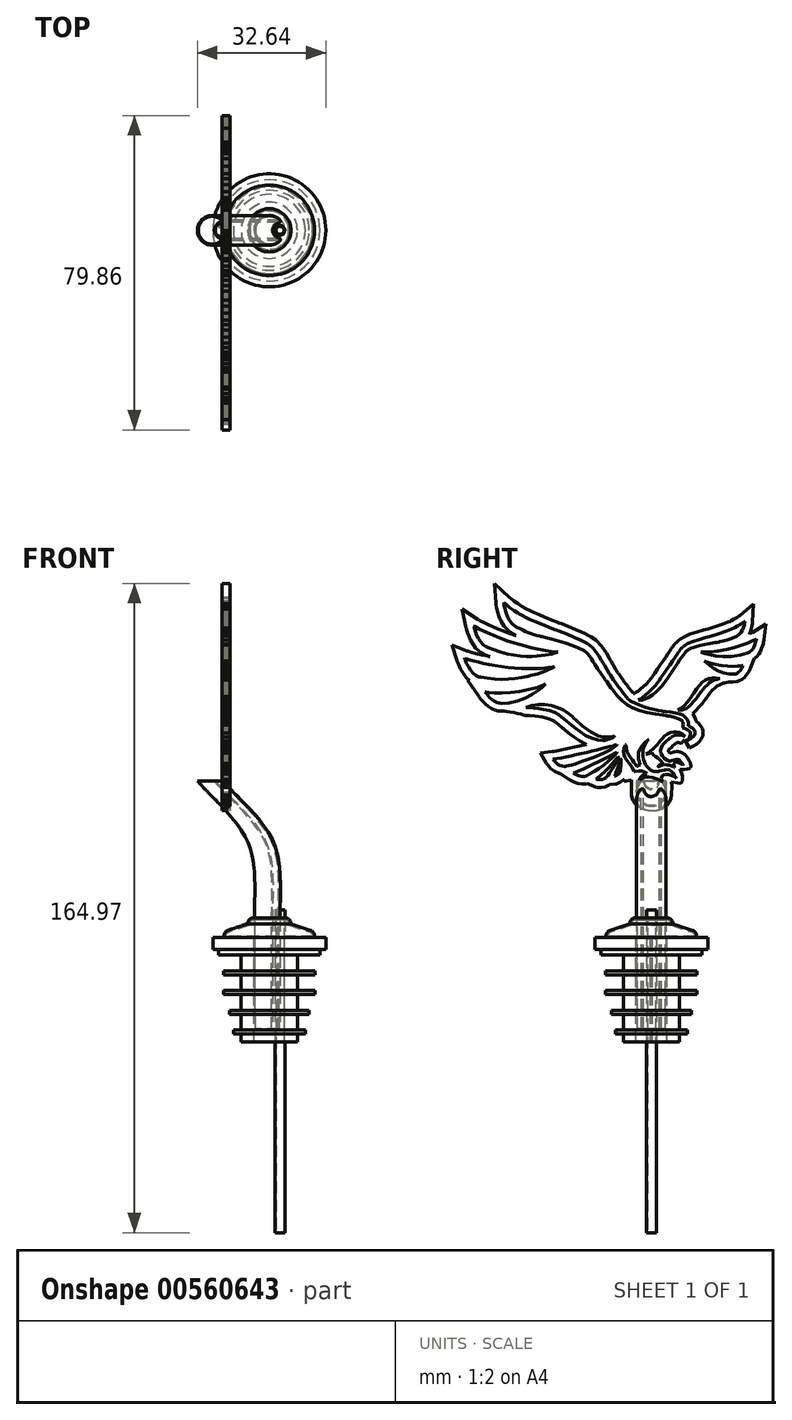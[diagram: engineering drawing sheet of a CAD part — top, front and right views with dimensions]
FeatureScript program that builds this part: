
annotation { "Feature Type Name" : "Feature", "Feature Type Description" : "" }
export const myFeature = defineFeature(function(context is Context, id is Id, definition is map)
    precondition{}
    {
        {
            var Q0;
            Q0=qCreatedBy(makeId("Top.planeOp"),FACE);
            var sketch = newSketch(context, id + "F0", { "sketchPlane" : qUnion([Q0])});
            skCircle(sketch, "E0", {"center": v(0, 0) * mm, "radius": 11.5 * mm});
            skSolve(sketch);
        }
        {
            var Q0;
            Q0=makeQuery(id+"F0.imprint","IMPRINT",FACE,{"disambiguationData":[TD([[makeQuery(id+"F0.imprint","IMPRINT",EDGE,{"derivedFrom":sQuery(id+"F0.wireOp",EDGE,"E0")}),1.0]])]});
            extrude(context, id + "F1", {"entities" : qUnion([Q0]), "depth" : 3.5 * mm, "offsetDistance" : 25 * mm});
        }
        {
            var Q0;
            Q0=makeQuery(id+"F1.opExtrude","CAP_FACE",FACE,{"disambiguationData":[OSD([sQuery(id+"F0.wireOp",EDGE,"E0")])],"isStart":false});
            chamfer(context, id + "F2", {"entities" : qUnion([Q0]), "chamferType" : ChamferType.TWO_OFFSETS, "width1" : 6 * mm, "oppositeDirection" : false, "width2" : 2 * mm, "tangentPropagation" : true});
        }
        {
            var Q0;
            Q0=makeQuery(id+"F1.opExtrude","CAP_FACE",FACE,{"disambiguationData":[OSD([sQuery(id+"F0.wireOp",EDGE,"E0")])],"isStart":false});
            var sketch = newSketch(context, id + "F3", { "sketchPlane" : qUnion([Q0])});
            skCircle(sketch, "E1", {"center": v(0, 0) * mm, "radius": 5.5 * mm});
            skSolve(sketch);
        }
        {
            var Q0;
            Q0=makeQuery(id+"F3.imprint","IMPRINT",FACE,{"disambiguationData":[TD([[makeQuery(id+"F3.imprint","IMPRINT",EDGE,{"derivedFrom":sQuery(id+"F3.wireOp",EDGE,"E1")}),1.0]])]});
            extrude(context, id + "F4", {"entities" : qUnion([Q0]), "operationType" : NewBodyOperationType.ADD, "depth" : 1.5 * mm, "offsetDistance" : 25 * mm});
        }
        {
            var Q0;
            Q0=makeQuery(id+"F4.opExtrude","CAP_EDGE",EDGE,{"disambiguationData":[OSD([sQuery(id+"F3.wireOp",EDGE,"E1")])],"isStart":false});
            fillet(context, id + "F5", {"entities" : qUnion([Q0]), "radius" : 1.5 * mm, "tangentPropagation" : true, "allowEdgeOverflow" : false});
        }
        {
            var Q0;
            {var subQ0=sQuery(id+"F0.wireOp",EDGE,"E0");Q0=makeQuery(id+"F2.opChamfer","BLEND_EDGE",EDGE,{"blendedFrom":[makeQuery(id+"F1.opExtrude","CAP_EDGE",EDGE,{"disambiguationData":[OSD([subQ0])],"isStart":false}),makeQuery(id+"F1.opExtrude","SWEPT_FACE",FACE,{"disambiguationData":[OSD([subQ0])]})],"blendedInto":[makeQuery(id+"F1.opExtrude","SWEPT_FACE",FACE,{"disambiguationData":[OSD([subQ0])]})]});}
            fillet(context, id + "F6", {"entities" : qUnion([Q0]), "radius" : 1.5 * mm, "tangentPropagation" : true, "allowEdgeOverflow" : false});
        }
        {
            var Q0;
            Q0=makeQuery(id+"F1.opExtrude","CAP_FACE",FACE,{"disambiguationData":[OSD([sQuery(id+"F0.wireOp",EDGE,"E0")])],"isStart":true});
            shell(context, id + "F7", {"entities" : qUnion([Q0]), "thickness" : 0.5 * mm});
        }
        {
            var Q0;
            Q0=qCreatedBy(makeId("Top.planeOp"),FACE);
            cPlane(context, id + "F8", {"entities" : qUnion([Q0]), "cplaneType" : CPlaneType.OFFSET, "offset" : 75 * mm, "oppositeDirection" : true, "width" : 150 * mm, "height" : 150 * mm});
        }
        {
            var Q0;
            Q0=qCreatedBy(id+"F8.planeOp",FACE);
            var sketch = newSketch(context, id + "F9", { "sketchPlane" : qUnion([Q0])});
            skCircle(sketch, "E2", {"center": v(2.7, 0) * mm, "radius": 1.25 * mm});
            skSolve(sketch);
        }
        {
            var Q0;
            Q0=makeQuery(id+"F9.imprint","IMPRINT",FACE,{"disambiguationData":[TD([[makeQuery(id+"F9.imprint","IMPRINT",EDGE,{"derivedFrom":sQuery(id+"F9.wireOp",EDGE,"E2")}),1.0]])]});
            extrude(context, id + "F10", {"entities" : qUnion([Q0]), "operationType" : NewBodyOperationType.ADD, "depth" : 82 * mm, "offsetDistance" : 25 * mm});
        }
        {
            var Q0;
            Q0=makeQuery(id+"F10.opExtrude","CAP_FACE",FACE,{"disambiguationData":[OSD([sQuery(id+"F9.wireOp",EDGE,"E2")])],"isStart":false});
            var Q1;
            Q1=makeQuery(id+"F10.opExtrude","CAP_FACE",FACE,{"disambiguationData":[OSD([sQuery(id+"F9.wireOp",EDGE,"E2")])],"isStart":true});
            shell(context, id + "F11", {"entities" : qUnion([Q0, Q1]), "thickness" : 0.25 * mm});
        }
        {
            var Q0;
            Q0=qCreatedBy(makeId("Top.planeOp"),FACE);
            cPlane(context, id + "F12", {"entities" : qUnion([Q0]), "cplaneType" : CPlaneType.OFFSET, "offset" : 23 * mm, "oppositeDirection" : true, "width" : 150 * mm, "height" : 150 * mm});
        }
        {
            var Q0;
            Q0=qCreatedBy(id+"F12.planeOp",FACE);
            var sketch = newSketch(context, id + "F13", { "sketchPlane" : qUnion([Q0])});
            skArc(sketch, "E3", {"start": v(2.59, 2.71) * mm, "mid": v(-3.75, 0) * mm, "end": v(2.59, -2.71) * mm});
            skArc(sketch, "E4", {"start": v(2.34, 1.86) * mm, "mid": v(0.82, 0) * mm, "end": v(2.34, -1.86) * mm});
            skPoint(sketch, "E5.visualSharp", {"position": v(3.28, 1.81) * mm});
            skArc(sketch, "E5.filletArc", {"start": v(2.34, 1.86) * mm, "mid": v(2.72, 2.21) * mm, "end": v(2.59, 2.71) * mm});
            skPoint(sketch, "E6.visualSharp", {"position": v(3.28, -1.81) * mm});
            skArc(sketch, "E6.filletArc", {"start": v(2.59, -2.71) * mm, "mid": v(2.72, -2.21) * mm, "end": v(2.34, -1.86) * mm});
            skSolve(sketch);
        }
        {
            var Q0;
            Q0=qCreatedBy(makeId("Top.planeOp"),FACE);
            cPlane(context, id + "F14", {"entities" : qUnion([Q0]), "cplaneType" : CPlaneType.OFFSET, "offset" : 15 * mm, "width" : 150 * mm, "height" : 150 * mm});
        }
        {
            var Q0;
            Q0=qCreatedBy(makeId("Front.planeOp"),FACE);
            var sketch = newSketch(context, id + "F15", { "sketchPlane" : qUnion([Q0])});
            skFitSpline(sketch, "E7", {"points": [v(0, -23.23) * mm, v(0, 6.5) * mm, v(0, 15.7) * mm, v(-2.95, 26.7) * mm, v(-14.54, 39.77) * mm], "startDerivative": vector(-0.7, 126.33) * mm, "endDerivative": vector(-30.29, 36.58) * mm});
            skSolve(sketch);
        }
        {
            var Q0;
            Q0=makeQuery(id+"F13.imprint","IMPRINT",FACE,{"disambiguationData":[TD([[makeQuery(id+"F13.imprint","IMPRINT",EDGE,{"derivedFrom":sQuery(id+"F13.wireOp",EDGE,"E3")}),1.0]])]});
            var Q1;
            Q1=sQuery(id+"F15.wireOp",EDGE,"E7");
            sweep(context, id + "F16", {"operationType" : NewBodyOperationType.ADD, "profiles" : qUnion([Q0]), "path" : qUnion([Q1]), "keepProfileOrientation" : true});
        }
        {
            var Q0;
            Q0=makeQuery(id+"F16.opSweep","CAP_FACE",FACE,{"disambiguationData":[OSD([sQuery(id+"F13.wireOp",EDGE,"E3"),sQuery(id+"F13.wireOp",EDGE,"E4"),sQuery(id+"F13.wireOp",EDGE,"E5.filletArc"),sQuery(id+"F13.wireOp",EDGE,"E6.filletArc"),sQuery(id+"F15.wireOp",VERTEX,"E7.end")])],"isStart":false});
            var Q1;
            Q1=makeQuery(id+"F16.opSweep","CAP_FACE",FACE,{"disambiguationData":[OSD([sQuery(id+"F13.wireOp",EDGE,"E3"),sQuery(id+"F13.wireOp",EDGE,"E4"),sQuery(id+"F13.wireOp",EDGE,"E5.filletArc"),sQuery(id+"F13.wireOp",EDGE,"E6.filletArc"),sQuery(id+"F15.wireOp",VERTEX,"E7.start")])],"isStart":true});
            shell(context, id + "F17", {"entities" : qUnion([Q0, Q1]), "thickness" : 0.2 * mm});
        }
        {
            var Q0;
            Q0=qCreatedBy(makeId("Right.planeOp"),FACE);
            var sketch = newSketch(context, id + "F18", { "sketchPlane" : qUnion([Q0])});
            skLineSegment(sketch, "E8", {"start": v(-3.93, -22.94) * mm, "end": v(-3.93, 0) * mm});
            skLineSegment(sketch, "E9", {"start": v(-3.93, 0) * mm, "end": v(-14.35, 0) * mm});
            skLineSegment(sketch, "E10", {"start": v(-14.35, 0) * mm, "end": v(-14.35, -3) * mm});
            skLineSegment(sketch, "E11", {"start": v(-14.35, -3) * mm, "end": v(-12.85, -3) * mm});
            skLineSegment(sketch, "E12", {"start": v(-12.85, -3) * mm, "end": v(-12.85, -4.5) * mm});
            skLineSegment(sketch, "E13", {"start": v(-12.85, -4.5) * mm, "end": v(-7.14, -4.5) * mm});
            skLineSegment(sketch, "E14", {"start": v(-7.14, -4.5) * mm, "end": v(-7.14, -8.5) * mm});
            skLineSegment(sketch, "E15", {"start": v(-7.14, -8.5) * mm, "end": v(-11.64, -8.5) * mm});
            skLineSegment(sketch, "E16", {"start": v(-11.64, -8.5) * mm, "end": v(-11.64, -9.5) * mm});
            skLineSegment(sketch, "E17", {"start": v(-11.64, -9.5) * mm, "end": v(-7.14, -9.5) * mm});
            skLineSegment(sketch, "E18", {"start": v(-7.14, -9.5) * mm, "end": v(-7.14, -13.5) * mm});
            skLineSegment(sketch, "E19", {"start": v(-7.14, -13.5) * mm, "end": v(-11.64, -13.5) * mm});
            skLineSegment(sketch, "E20", {"start": v(-11.64, -13.5) * mm, "end": v(-11.64, -14.5) * mm});
            skLineSegment(sketch, "E21", {"start": v(-11.64, -14.5) * mm, "end": v(-7.14, -14.5) * mm});
            skLineSegment(sketch, "E22", {"start": v(-7.14, -14.5) * mm, "end": v(-7.14, -18.5) * mm});
            skLineSegment(sketch, "E23", {"start": v(-7.14, -18.5) * mm, "end": v(-10.14, -18.5) * mm});
            skLineSegment(sketch, "E24", {"start": v(-10.14, -18.5) * mm, "end": v(-10.14, -19.5) * mm});
            skLineSegment(sketch, "E25", {"start": v(-10.14, -19.5) * mm, "end": v(-7.14, -19.5) * mm});
            skLineSegment(sketch, "E26", {"start": v(-7.14, -19.5) * mm, "end": v(-7.14, -23.5) * mm});
            skLineSegment(sketch, "E27", {"start": v(-7.14, -23.5) * mm, "end": v(-9.14, -23.5) * mm});
            skLineSegment(sketch, "E28", {"start": v(-9.14, -23.5) * mm, "end": v(-9.14, -24.5) * mm});
            skLineSegment(sketch, "E29", {"start": v(-9.14, -24.5) * mm, "end": v(-7.14, -24.5) * mm});
            skLineSegment(sketch, "E30", {"start": v(-7.14, -24.5) * mm, "end": v(-7.14, -26.5) * mm});
            skLineSegment(sketch, "E31", {"start": v(-7.14, -26.5) * mm, "end": v(-3.93, -26.5) * mm});
            skLineSegment(sketch, "E32", {"start": v(-3.93, -26.5) * mm, "end": v(-3.93, -22.94) * mm});
            skLineSegment(sketch, "E33", {"start": v(0, 0) * mm, "end": v(0, -26.54) * mm});
            skSolve(sketch);
        }
        {
            var Q0;
            Q0=makeQuery(id+"F18.imprint","IMPRINT",FACE,{"disambiguationData":[TD([[makeQuery(id+"F18.imprint","IMPRINT",EDGE,{"derivedFrom":sQuery(id+"F18.wireOp",EDGE,"E8")}),1.0]])]});
            var Q1;
            Q1=sQuery(id+"F18.wireOp",EDGE,"E33");
            revolve(context, id + "F19", {"operationType" : NewBodyOperationType.ADD, "entities" : qUnion([Q0]), "axis" : qUnion([Q1]), "revolveType" : RevolveType.FULL});
        }
        {
            var Q0;
            Q0=qCreatedBy(makeId("Right.planeOp"),FACE);
            cPlane(context, id + "F20", {"entities" : qUnion([Q0]), "cplaneType" : CPlaneType.OFFSET, "offset" : 12 * mm, "oppositeDirection" : true, "width" : 150 * mm, "height" : 150 * mm});
        }
        {
            var Q0;
            Q0=qCreatedBy(id+"F20.planeOp",FACE);
            var sketch = newSketch(context, id + "F21", { "sketchPlane" : qUnion([Q0])});
            skLineSegment(sketch, "E34", {"start": v(24.98, 72.56) * mm, "end": v(24.4, 72.32) * mm});
            skLineSegment(sketch, "E35", {"start": v(24.4, 72.32) * mm, "end": v(22.61, 71.8) * mm});
            skLineSegment(sketch, "E36", {"start": v(22.61, 71.8) * mm, "end": v(20.35, 71.44) * mm});
            skLineSegment(sketch, "E37", {"start": v(20.35, 71.44) * mm, "end": v(18.25, 71.39) * mm});
            skLineSegment(sketch, "E38", {"start": v(18.25, 71.39) * mm, "end": v(16.38, 71.55) * mm});
            skLineSegment(sketch, "E39", {"start": v(16.38, 71.55) * mm, "end": v(14.81, 71.84) * mm});
            skLineSegment(sketch, "E40", {"start": v(14.81, 71.84) * mm, "end": v(13.6, 72.17) * mm});
            skLineSegment(sketch, "E41", {"start": v(13.6, 72.17) * mm, "end": v(12.84, 72.43) * mm});
            skLineSegment(sketch, "E42", {"start": v(12.84, 72.43) * mm, "end": v(12.57, 72.54) * mm});
            skLineSegment(sketch, "E43", {"start": v(12.57, 72.54) * mm, "end": v(13.1, 72.5) * mm});
            skLineSegment(sketch, "E44", {"start": v(13.1, 72.5) * mm, "end": v(14.73, 72.54) * mm});
            skLineSegment(sketch, "E45", {"start": v(14.73, 72.54) * mm, "end": v(16.92, 72.76) * mm});
            skLineSegment(sketch, "E46", {"start": v(16.92, 72.76) * mm, "end": v(19.08, 73.17) * mm});
            skLineSegment(sketch, "E47", {"start": v(19.08, 73.17) * mm, "end": v(21.13, 73.7) * mm});
            skLineSegment(sketch, "E48", {"start": v(21.13, 73.7) * mm, "end": v(22.98, 74.28) * mm});
            skLineSegment(sketch, "E49", {"start": v(22.98, 74.28) * mm, "end": v(24.57, 74.87) * mm});
            skLineSegment(sketch, "E50", {"start": v(24.57, 74.87) * mm, "end": v(25.82, 75.42) * mm});
            skLineSegment(sketch, "E51", {"start": v(25.82, 75.42) * mm, "end": v(26.46, 75.73) * mm});
            skLineSegment(sketch, "E52", {"start": v(26.46, 75.73) * mm, "end": v(26.66, 75.85) * mm});
            skLineSegment(sketch, "E53", {"start": v(26.66, 75.85) * mm, "end": v(26.64, 75.73) * mm});
            skLineSegment(sketch, "E54", {"start": v(26.64, 75.73) * mm, "end": v(26.58, 75.42) * mm});
            skLineSegment(sketch, "E55", {"start": v(26.58, 75.42) * mm, "end": v(26.47, 74.96) * mm});
            skLineSegment(sketch, "E56", {"start": v(26.47, 74.96) * mm, "end": v(26.3, 74.41) * mm});
            skLineSegment(sketch, "E57", {"start": v(26.3, 74.41) * mm, "end": v(26.08, 73.84) * mm});
            skLineSegment(sketch, "E58", {"start": v(26.08, 73.84) * mm, "end": v(25.8, 73.3) * mm});
            skLineSegment(sketch, "E59", {"start": v(25.8, 73.3) * mm, "end": v(25.43, 72.86) * mm});
            skLineSegment(sketch, "E60", {"start": v(25.43, 72.86) * mm, "end": v(25.1, 72.61) * mm});
            skLineSegment(sketch, "E61", {"start": v(25.1, 72.61) * mm, "end": v(24.98, 72.56) * mm});
            skLineSegment(sketch, "E62", {"start": v(21.4, 66.97) * mm, "end": v(21.02, 66.9) * mm});
            skLineSegment(sketch, "E63", {"start": v(21.02, 66.9) * mm, "end": v(19.86, 66.91) * mm});
            skLineSegment(sketch, "E64", {"start": v(19.86, 66.91) * mm, "end": v(18.4, 67.2) * mm});
            skLineSegment(sketch, "E65", {"start": v(18.4, 67.2) * mm, "end": v(17.06, 67.72) * mm});
            skLineSegment(sketch, "E66", {"start": v(17.06, 67.72) * mm, "end": v(15.87, 68.38) * mm});
            skLineSegment(sketch, "E67", {"start": v(15.87, 68.38) * mm, "end": v(14.88, 69.07) * mm});
            skLineSegment(sketch, "E68", {"start": v(14.88, 69.07) * mm, "end": v(14.13, 69.69) * mm});
            skLineSegment(sketch, "E69", {"start": v(14.13, 69.69) * mm, "end": v(13.65, 70.13) * mm});
            skLineSegment(sketch, "E70", {"start": v(13.65, 70.13) * mm, "end": v(13.48, 70.3) * mm});
            skLineSegment(sketch, "E71", {"start": v(13.48, 70.3) * mm, "end": v(13.81, 70.13) * mm});
            skLineSegment(sketch, "E72", {"start": v(13.81, 70.13) * mm, "end": v(14.87, 69.72) * mm});
            skLineSegment(sketch, "E73", {"start": v(14.87, 69.72) * mm, "end": v(16.36, 69.31) * mm});
            skLineSegment(sketch, "E74", {"start": v(16.36, 69.31) * mm, "end": v(17.87, 69.05) * mm});
            skLineSegment(sketch, "E75", {"start": v(17.87, 69.05) * mm, "end": v(19.33, 68.92) * mm});
            skLineSegment(sketch, "E76", {"start": v(19.33, 68.92) * mm, "end": v(20.67, 68.88) * mm});
            skLineSegment(sketch, "E77", {"start": v(20.67, 68.88) * mm, "end": v(21.83, 68.93) * mm});
            skLineSegment(sketch, "E78", {"start": v(21.83, 68.93) * mm, "end": v(22.73, 69.02) * mm});
            skLineSegment(sketch, "E79", {"start": v(22.73, 69.02) * mm, "end": v(23.17, 69.1) * mm});
            skLineSegment(sketch, "E80", {"start": v(23.17, 69.1) * mm, "end": v(23.31, 69.15) * mm});
            skLineSegment(sketch, "E81", {"start": v(23.31, 69.15) * mm, "end": v(23.27, 69.06) * mm});
            skLineSegment(sketch, "E82", {"start": v(23.27, 69.06) * mm, "end": v(23.17, 68.83) * mm});
            skLineSegment(sketch, "E83", {"start": v(23.17, 68.83) * mm, "end": v(23, 68.5) * mm});
            skLineSegment(sketch, "E84", {"start": v(23, 68.5) * mm, "end": v(22.77, 68.12) * mm});
            skLineSegment(sketch, "E85", {"start": v(22.77, 68.12) * mm, "end": v(22.5, 67.74) * mm});
            skLineSegment(sketch, "E86", {"start": v(22.5, 67.74) * mm, "end": v(22.17, 67.38) * mm});
            skLineSegment(sketch, "E87", {"start": v(22.17, 67.38) * mm, "end": v(21.8, 67.11) * mm});
            skLineSegment(sketch, "E88", {"start": v(21.8, 67.11) * mm, "end": v(21.5, 66.98) * mm});
            skLineSegment(sketch, "E89", {"start": v(21.5, 66.98) * mm, "end": v(21.4, 66.97) * mm});
            skLineSegment(sketch, "E90", {"start": v(11.79, 61.24) * mm, "end": v(11.67, 61.08) * mm});
            skLineSegment(sketch, "E91", {"start": v(11.67, 61.08) * mm, "end": v(11.3, 60.59) * mm});
            skLineSegment(sketch, "E92", {"start": v(11.3, 60.59) * mm, "end": v(10.75, 59.91) * mm});
            skLineSegment(sketch, "E93", {"start": v(10.75, 59.91) * mm, "end": v(10.16, 59.26) * mm});
            skLineSegment(sketch, "E94", {"start": v(10.16, 59.26) * mm, "end": v(9.53, 58.67) * mm});
            skLineSegment(sketch, "E95", {"start": v(9.53, 58.67) * mm, "end": v(8.87, 58.2) * mm});
            skLineSegment(sketch, "E96", {"start": v(8.87, 58.2) * mm, "end": v(8.18, 57.86) * mm});
            skLineSegment(sketch, "E97", {"start": v(8.18, 57.86) * mm, "end": v(7.48, 57.72) * mm});
            skLineSegment(sketch, "E98", {"start": v(7.48, 57.72) * mm, "end": v(6.93, 57.76) * mm});
            skLineSegment(sketch, "E99", {"start": v(6.93, 57.76) * mm, "end": v(6.76, 57.81) * mm});
            skLineSegment(sketch, "E100", {"start": v(6.76, 57.81) * mm, "end": v(6.94, 57.86) * mm});
            skLineSegment(sketch, "E101", {"start": v(6.94, 57.86) * mm, "end": v(7.45, 58.12) * mm});
            skLineSegment(sketch, "E102", {"start": v(7.45, 58.12) * mm, "end": v(8.3, 58.8) * mm});
            skLineSegment(sketch, "E103", {"start": v(8.3, 58.8) * mm, "end": v(9.34, 60) * mm});
            skLineSegment(sketch, "E104", {"start": v(9.34, 60) * mm, "end": v(10.32, 61.38) * mm});
            skLineSegment(sketch, "E105", {"start": v(10.32, 61.38) * mm, "end": v(10.62, 61.86) * mm});
            skLineSegment(sketch, "E106", {"start": v(10.62, 61.86) * mm, "end": v(10.82, 62.17) * mm});
            skLineSegment(sketch, "E107", {"start": v(10.82, 62.17) * mm, "end": v(11.44, 63.08) * mm});
            skLineSegment(sketch, "E108", {"start": v(11.44, 63.08) * mm, "end": v(12.22, 64.08) * mm});
            skLineSegment(sketch, "E109", {"start": v(12.22, 64.08) * mm, "end": v(12.99, 64.86) * mm});
            skLineSegment(sketch, "E110", {"start": v(12.99, 64.86) * mm, "end": v(13.77, 65.43) * mm});
            skLineSegment(sketch, "E111", {"start": v(13.77, 65.43) * mm, "end": v(14.58, 65.8) * mm});
            skLineSegment(sketch, "E112", {"start": v(14.58, 65.8) * mm, "end": v(15.45, 65.98) * mm});
            skLineSegment(sketch, "E113", {"start": v(15.45, 65.98) * mm, "end": v(16.4, 65.98) * mm});
            skLineSegment(sketch, "E114", {"start": v(16.4, 65.98) * mm, "end": v(17.2, 65.85) * mm});
            skLineSegment(sketch, "E115", {"start": v(17.2, 65.85) * mm, "end": v(17.45, 65.8) * mm});
            skLineSegment(sketch, "E116", {"start": v(17.45, 65.8) * mm, "end": v(17.26, 65.74) * mm});
            skLineSegment(sketch, "E117", {"start": v(17.26, 65.74) * mm, "end": v(16.68, 65.6) * mm});
            skLineSegment(sketch, "E118", {"start": v(16.68, 65.6) * mm, "end": v(16.02, 65.38) * mm});
            skLineSegment(sketch, "E119", {"start": v(16.02, 65.38) * mm, "end": v(15.4, 65.1) * mm});
            skLineSegment(sketch, "E120", {"start": v(15.4, 65.1) * mm, "end": v(14.82, 64.72) * mm});
            skLineSegment(sketch, "E121", {"start": v(14.82, 64.72) * mm, "end": v(14.21, 64.18) * mm});
            skLineSegment(sketch, "E122", {"start": v(14.21, 64.18) * mm, "end": v(13.53, 63.46) * mm});
            skLineSegment(sketch, "E123", {"start": v(13.53, 63.46) * mm, "end": v(12.74, 62.49) * mm});
            skLineSegment(sketch, "E124", {"start": v(12.74, 62.49) * mm, "end": v(12.02, 61.56) * mm});
            skLineSegment(sketch, "E125", {"start": v(12.02, 61.56) * mm, "end": v(11.79, 61.24) * mm});
            skLineSegment(sketch, "E126", {"start": v(8.94, 49.98) * mm, "end": v(8.99, 50.02) * mm});
            skLineSegment(sketch, "E127", {"start": v(8.99, 50.02) * mm, "end": v(9.12, 50.13) * mm});
            skLineSegment(sketch, "E128", {"start": v(9.12, 50.13) * mm, "end": v(9.3, 50.32) * mm});
            skLineSegment(sketch, "E129", {"start": v(9.3, 50.32) * mm, "end": v(9.5, 50.55) * mm});
            skLineSegment(sketch, "E130", {"start": v(9.5, 50.55) * mm, "end": v(9.7, 50.84) * mm});
            skLineSegment(sketch, "E131", {"start": v(9.7, 50.84) * mm, "end": v(9.86, 51.16) * mm});
            skLineSegment(sketch, "E132", {"start": v(9.86, 51.16) * mm, "end": v(9.95, 51.5) * mm});
            skLineSegment(sketch, "E133", {"start": v(9.95, 51.5) * mm, "end": v(9.96, 51.79) * mm});
            skLineSegment(sketch, "E134", {"start": v(9.96, 51.79) * mm, "end": v(9.95, 51.87) * mm});
            skLineSegment(sketch, "E135", {"start": v(9.95, 51.87) * mm, "end": v(9.93, 52) * mm});
            skLineSegment(sketch, "E136", {"start": v(9.93, 52) * mm, "end": v(9.75, 52.34) * mm});
            skLineSegment(sketch, "E137", {"start": v(9.75, 52.34) * mm, "end": v(9.35, 52.69) * mm});
            skLineSegment(sketch, "E138", {"start": v(9.35, 52.69) * mm, "end": v(8.75, 52.97) * mm});
            skLineSegment(sketch, "E139", {"start": v(8.75, 52.97) * mm, "end": v(8.13, 53.18) * mm});
            skLineSegment(sketch, "E140", {"start": v(8.13, 53.18) * mm, "end": v(7.93, 53.25) * mm});
            skLineSegment(sketch, "E141", {"start": v(7.93, 53.25) * mm, "end": v(7.97, 53.39) * mm});
            skLineSegment(sketch, "E142", {"start": v(7.97, 53.39) * mm, "end": v(8.06, 53.73) * mm});
            skLineSegment(sketch, "E143", {"start": v(8.06, 53.73) * mm, "end": v(8.1, 54.16) * mm});
            skLineSegment(sketch, "E144", {"start": v(8.1, 54.16) * mm, "end": v(8.08, 54.47) * mm});
            skLineSegment(sketch, "E145", {"start": v(8.08, 54.47) * mm, "end": v(8.05, 54.56) * mm});
            skLineSegment(sketch, "E146", {"start": v(8.05, 54.56) * mm, "end": v(8, 54.7) * mm});
            skLineSegment(sketch, "E147", {"start": v(8, 54.7) * mm, "end": v(7.72, 55.06) * mm});
            skLineSegment(sketch, "E148", {"start": v(7.72, 55.06) * mm, "end": v(7.07, 55.52) * mm});
            skLineSegment(sketch, "E149", {"start": v(7.07, 55.52) * mm, "end": v(5.99, 55.93) * mm});
            skLineSegment(sketch, "E150", {"start": v(5.99, 55.93) * mm, "end": v(4.77, 56.21) * mm});
            skLineSegment(sketch, "E151", {"start": v(4.77, 56.21) * mm, "end": v(4.36, 56.28) * mm});
            skLineSegment(sketch, "E152", {"start": v(4.36, 56.28) * mm, "end": v(4.33, 56.28) * mm});
            skLineSegment(sketch, "E153", {"start": v(4.33, 56.28) * mm, "end": v(3.99, 56.33) * mm});
            skLineSegment(sketch, "E154", {"start": v(3.99, 56.33) * mm, "end": v(3.95, 56.34) * mm});
            skLineSegment(sketch, "E155", {"start": v(3.95, 56.34) * mm, "end": v(3.93, 56.34) * mm});
            skLineSegment(sketch, "E156", {"start": v(3.93, 56.34) * mm, "end": v(3.66, 56.37) * mm});
            skLineSegment(sketch, "E157", {"start": v(3.66, 56.37) * mm, "end": v(3.63, 56.37) * mm});
            skLineSegment(sketch, "E158", {"start": v(3.63, 56.37) * mm, "end": v(2.98, 56.47) * mm});
            skLineSegment(sketch, "E159", {"start": v(2.98, 56.47) * mm, "end": v(1.04, 56.77) * mm});
            skLineSegment(sketch, "E160", {"start": v(1.04, 56.77) * mm, "end": v(-1.15, 57.18) * mm});
            skLineSegment(sketch, "E161", {"start": v(-1.15, 57.18) * mm, "end": v(-3.03, 57.66) * mm});
            skLineSegment(sketch, "E162", {"start": v(-3.03, 57.66) * mm, "end": v(-4.66, 58.28) * mm});
            skLineSegment(sketch, "E163", {"start": v(-4.66, 58.28) * mm, "end": v(-6.1, 59.09) * mm});
            skLineSegment(sketch, "E164", {"start": v(-6.1, 59.09) * mm, "end": v(-7.45, 60.15) * mm});
            skLineSegment(sketch, "E165", {"start": v(-7.45, 60.15) * mm, "end": v(-8.75, 61.52) * mm});
            skLineSegment(sketch, "E166", {"start": v(-8.75, 61.52) * mm, "end": v(-9.77, 62.81) * mm});
            skLineSegment(sketch, "E167", {"start": v(-9.77, 62.81) * mm, "end": v(-10.09, 63.26) * mm});
            skLineSegment(sketch, "E168", {"start": v(-10.09, 63.26) * mm, "end": v(-10.2, 63.43) * mm});
            skLineSegment(sketch, "E169", {"start": v(-10.2, 63.43) * mm, "end": v(-11.3, 64.99) * mm});
            skLineSegment(sketch, "E170", {"start": v(-11.3, 64.99) * mm, "end": v(-11.4, 65.13) * mm});
            skLineSegment(sketch, "E171", {"start": v(-11.4, 65.13) * mm, "end": v(-11.41, 65.15) * mm});
            skLineSegment(sketch, "E172", {"start": v(-11.41, 65.15) * mm, "end": v(-11.57, 65.37) * mm});
            skLineSegment(sketch, "E173", {"start": v(-11.57, 65.37) * mm, "end": v(-11.59, 65.4) * mm});
            skLineSegment(sketch, "E174", {"start": v(-11.59, 65.4) * mm, "end": v(-11.9, 65.81) * mm});
            skLineSegment(sketch, "E175", {"start": v(-11.9, 65.81) * mm, "end": v(-12.8, 67.08) * mm});
            skLineSegment(sketch, "E176", {"start": v(-12.8, 67.08) * mm, "end": v(-13.7, 68.4) * mm});
            skLineSegment(sketch, "E177", {"start": v(-13.7, 68.4) * mm, "end": v(-14.35, 69.39) * mm});
            skLineSegment(sketch, "E178", {"start": v(-14.35, 69.39) * mm, "end": v(-14.81, 70.14) * mm});
            skLineSegment(sketch, "E179", {"start": v(-14.81, 70.14) * mm, "end": v(-15.16, 70.73) * mm});
            skLineSegment(sketch, "E180", {"start": v(-15.16, 70.73) * mm, "end": v(-15.46, 71.2) * mm});
            skLineSegment(sketch, "E181", {"start": v(-15.46, 71.2) * mm, "end": v(-15.78, 71.64) * mm});
            skLineSegment(sketch, "E182", {"start": v(-15.78, 71.64) * mm, "end": v(-16.1, 72) * mm});
            skLineSegment(sketch, "E183", {"start": v(-16.1, 72) * mm, "end": v(-16.2, 72.12) * mm});
            skLineSegment(sketch, "E184", {"start": v(-16.2, 72.12) * mm, "end": v(-16.4, 72.33) * mm});
            skLineSegment(sketch, "E185", {"start": v(-16.4, 72.33) * mm, "end": v(-17.14, 72.85) * mm});
            skLineSegment(sketch, "E186", {"start": v(-17.14, 72.85) * mm, "end": v(-18.47, 73.54) * mm});
            skLineSegment(sketch, "E187", {"start": v(-18.47, 73.54) * mm, "end": v(-20.07, 74.2) * mm});
            skLineSegment(sketch, "E188", {"start": v(-20.07, 74.2) * mm, "end": v(-21.83, 74.79) * mm});
            skLineSegment(sketch, "E189", {"start": v(-21.83, 74.79) * mm, "end": v(-23.63, 75.32) * mm});
            skLineSegment(sketch, "E190", {"start": v(-23.63, 75.32) * mm, "end": v(-25.35, 75.79) * mm});
            skLineSegment(sketch, "E191", {"start": v(-25.35, 75.79) * mm, "end": v(-26.89, 76.18) * mm});
            skLineSegment(sketch, "E192", {"start": v(-26.89, 76.18) * mm, "end": v(-27.8, 76.4) * mm});
            skLineSegment(sketch, "E193", {"start": v(-27.8, 76.4) * mm, "end": v(-28.11, 76.48) * mm});
            skLineSegment(sketch, "E194", {"start": v(-28.11, 76.48) * mm, "end": v(-28.35, 76.54) * mm});
            skLineSegment(sketch, "E195", {"start": v(-28.35, 76.54) * mm, "end": v(-29.08, 76.73) * mm});
            skLineSegment(sketch, "E196", {"start": v(-29.08, 76.73) * mm, "end": v(-29.9, 76.96) * mm});
            skLineSegment(sketch, "E197", {"start": v(-29.9, 76.96) * mm, "end": v(-30.62, 77.2) * mm});
            skLineSegment(sketch, "E198", {"start": v(-30.62, 77.2) * mm, "end": v(-31.3, 77.44) * mm});
            skLineSegment(sketch, "E199", {"start": v(-31.3, 77.44) * mm, "end": v(-31.95, 77.72) * mm});
            skLineSegment(sketch, "E200", {"start": v(-31.95, 77.72) * mm, "end": v(-32.65, 78.05) * mm});
            skLineSegment(sketch, "E201", {"start": v(-32.65, 78.05) * mm, "end": v(-33.41, 78.45) * mm});
            skLineSegment(sketch, "E202", {"start": v(-33.41, 78.45) * mm, "end": v(-34.08, 78.8) * mm});
            skLineSegment(sketch, "E203", {"start": v(-34.08, 78.8) * mm, "end": v(-34.3, 78.92) * mm});
            skLineSegment(sketch, "E204", {"start": v(-34.3, 78.92) * mm, "end": v(-34.56, 79.06) * mm});
            skLineSegment(sketch, "E205", {"start": v(-34.56, 79.06) * mm, "end": v(-35.25, 79.62) * mm});
            skLineSegment(sketch, "E206", {"start": v(-35.25, 79.62) * mm, "end": v(-36, 80.53) * mm});
            skLineSegment(sketch, "E207", {"start": v(-36, 80.53) * mm, "end": v(-36.56, 81.54) * mm});
            skLineSegment(sketch, "E208", {"start": v(-36.56, 81.54) * mm, "end": v(-36.96, 82.58) * mm});
            skLineSegment(sketch, "E209", {"start": v(-36.96, 82.58) * mm, "end": v(-37.23, 83.54) * mm});
            skLineSegment(sketch, "E210", {"start": v(-37.23, 83.54) * mm, "end": v(-37.39, 84.34) * mm});
            skLineSegment(sketch, "E211", {"start": v(-37.39, 84.34) * mm, "end": v(-37.47, 84.9) * mm});
            skLineSegment(sketch, "E212", {"start": v(-37.47, 84.9) * mm, "end": v(-37.49, 85.1) * mm});
            skLineSegment(sketch, "E213", {"start": v(-37.49, 85.1) * mm, "end": v(-37.34, 84.96) * mm});
            skLineSegment(sketch, "E214", {"start": v(-37.34, 84.96) * mm, "end": v(-36.86, 84.56) * mm});
            skLineSegment(sketch, "E215", {"start": v(-36.86, 84.56) * mm, "end": v(-35.98, 83.89) * mm});
            skLineSegment(sketch, "E216", {"start": v(-35.98, 83.89) * mm, "end": v(-34.87, 83.1) * mm});
            skLineSegment(sketch, "E217", {"start": v(-34.87, 83.1) * mm, "end": v(-33.9, 82.44) * mm});
            skLineSegment(sketch, "E218", {"start": v(-33.9, 82.44) * mm, "end": v(-33.56, 82.23) * mm});
            skLineSegment(sketch, "E219", {"start": v(-33.56, 82.23) * mm, "end": v(-33.49, 82.19) * mm});
            skLineSegment(sketch, "E220", {"start": v(-33.49, 82.19) * mm, "end": v(-33.25, 82.06) * mm});
            skLineSegment(sketch, "E221", {"start": v(-33.25, 82.06) * mm, "end": v(-32.7, 81.76) * mm});
            skLineSegment(sketch, "E222", {"start": v(-32.7, 81.76) * mm, "end": v(-31.88, 81.35) * mm});
            skLineSegment(sketch, "E223", {"start": v(-31.88, 81.35) * mm, "end": v(-30.82, 80.83) * mm});
            skLineSegment(sketch, "E224", {"start": v(-30.82, 80.83) * mm, "end": v(-29.5, 80.24) * mm});
            skLineSegment(sketch, "E225", {"start": v(-29.5, 80.24) * mm, "end": v(-27.96, 79.57) * mm});
            skLineSegment(sketch, "E226", {"start": v(-27.96, 79.57) * mm, "end": v(-26.16, 78.86) * mm});
            skLineSegment(sketch, "E227", {"start": v(-26.16, 78.86) * mm, "end": v(-24.64, 78.28) * mm});
            skLineSegment(sketch, "E228", {"start": v(-24.64, 78.28) * mm, "end": v(-24.13, 78.1) * mm});
            skLineSegment(sketch, "E229", {"start": v(-24.13, 78.1) * mm, "end": v(-23.47, 77.86) * mm});
            skLineSegment(sketch, "E230", {"start": v(-23.47, 77.86) * mm, "end": v(-21.49, 77.1) * mm});
            skLineSegment(sketch, "E231", {"start": v(-21.49, 77.1) * mm, "end": v(-19.5, 76.27) * mm});
            skLineSegment(sketch, "E232", {"start": v(-19.5, 76.27) * mm, "end": v(-17.98, 75.57) * mm});
            skLineSegment(sketch, "E233", {"start": v(-17.98, 75.57) * mm, "end": v(-17.04, 75.1) * mm});
            skLineSegment(sketch, "E234", {"start": v(-17.04, 75.1) * mm, "end": v(-16.72, 74.96) * mm});
            skLineSegment(sketch, "E235", {"start": v(-16.72, 74.96) * mm, "end": v(-16.46, 74.83) * mm});
            skLineSegment(sketch, "E236", {"start": v(-16.46, 74.83) * mm, "end": v(-15.71, 74.34) * mm});
            skLineSegment(sketch, "E237", {"start": v(-15.71, 74.34) * mm, "end": v(-14.82, 73.52) * mm});
            skLineSegment(sketch, "E238", {"start": v(-14.82, 73.52) * mm, "end": v(-14.02, 72.55) * mm});
            skLineSegment(sketch, "E239", {"start": v(-14.02, 72.55) * mm, "end": v(-13.3, 71.48) * mm});
            skLineSegment(sketch, "E240", {"start": v(-13.3, 71.48) * mm, "end": v(-12.62, 70.34) * mm});
            skLineSegment(sketch, "E241", {"start": v(-12.62, 70.34) * mm, "end": v(-11.96, 69.18) * mm});
            skLineSegment(sketch, "E242", {"start": v(-11.96, 69.18) * mm, "end": v(-11.3, 68.04) * mm});
            skLineSegment(sketch, "E243", {"start": v(-11.3, 68.04) * mm, "end": v(-10.81, 67.24) * mm});
            skLineSegment(sketch, "E244", {"start": v(-10.81, 67.24) * mm, "end": v(-10.64, 66.98) * mm});
            skLineSegment(sketch, "E245", {"start": v(-10.64, 66.98) * mm, "end": v(-10.44, 66.69) * mm});
            skLineSegment(sketch, "E246", {"start": v(-10.44, 66.69) * mm, "end": v(-9.58, 65.4) * mm});
            skLineSegment(sketch, "E247", {"start": v(-9.58, 65.4) * mm, "end": v(-8.77, 64.24) * mm});
            skLineSegment(sketch, "E248", {"start": v(-8.77, 64.24) * mm, "end": v(-8.6, 64.01) * mm});
            skLineSegment(sketch, "E249", {"start": v(-8.6, 64.01) * mm, "end": v(-8.42, 63.77) * mm});
            skLineSegment(sketch, "E250", {"start": v(-8.42, 63.77) * mm, "end": v(-7.88, 63.07) * mm});
            skLineSegment(sketch, "E251", {"start": v(-7.88, 63.07) * mm, "end": v(-7.32, 62.31) * mm});
            skLineSegment(sketch, "E252", {"start": v(-7.32, 62.31) * mm, "end": v(-6.86, 61.73) * mm});
            skLineSegment(sketch, "E253", {"start": v(-6.86, 61.73) * mm, "end": v(-6.5, 61.27) * mm});
            skLineSegment(sketch, "E254", {"start": v(-6.5, 61.27) * mm, "end": v(-6.19, 60.91) * mm});
            skLineSegment(sketch, "E255", {"start": v(-6.19, 60.91) * mm, "end": v(-5.9, 60.63) * mm});
            skLineSegment(sketch, "E256", {"start": v(-5.9, 60.63) * mm, "end": v(-5.62, 60.37) * mm});
            skLineSegment(sketch, "E257", {"start": v(-5.62, 60.37) * mm, "end": v(-5.38, 60.19) * mm});
            skLineSegment(sketch, "E258", {"start": v(-5.38, 60.19) * mm, "end": v(-5.3, 60.13) * mm});
            skLineSegment(sketch, "E259", {"start": v(-5.3, 60.13) * mm, "end": v(-5.04, 59.96) * mm});
            skLineSegment(sketch, "E260", {"start": v(-5.04, 59.96) * mm, "end": v(-4.2, 59.52) * mm});
            skLineSegment(sketch, "E261", {"start": v(-4.2, 59.52) * mm, "end": v(-2.98, 59) * mm});
            skLineSegment(sketch, "E262", {"start": v(-2.98, 59) * mm, "end": v(-1.71, 58.57) * mm});
            skLineSegment(sketch, "E263", {"start": v(-1.71, 58.57) * mm, "end": v(-0.45, 58.2) * mm});
            skLineSegment(sketch, "E264", {"start": v(-0.45, 58.2) * mm, "end": v(0.74, 57.92) * mm});
            skLineSegment(sketch, "E265", {"start": v(0.74, 57.92) * mm, "end": v(1.8, 57.7) * mm});
            skLineSegment(sketch, "E266", {"start": v(1.8, 57.7) * mm, "end": v(2.66, 57.54) * mm});
            skLineSegment(sketch, "E267", {"start": v(2.66, 57.54) * mm, "end": v(3.13, 57.47) * mm});
            skLineSegment(sketch, "E268", {"start": v(3.13, 57.47) * mm, "end": v(3.28, 57.44) * mm});
            skLineSegment(sketch, "E269", {"start": v(3.28, 57.44) * mm, "end": v(3.67, 57.39) * mm});
            skLineSegment(sketch, "E270", {"start": v(3.67, 57.39) * mm, "end": v(4.85, 57.23) * mm});
            skLineSegment(sketch, "E271", {"start": v(4.85, 57.23) * mm, "end": v(6.19, 57.01) * mm});
            skLineSegment(sketch, "E272", {"start": v(6.19, 57.01) * mm, "end": v(7.3, 56.73) * mm});
            skLineSegment(sketch, "E273", {"start": v(7.3, 56.73) * mm, "end": v(7.97, 56.46) * mm});
            skLineSegment(sketch, "E274", {"start": v(7.97, 56.46) * mm, "end": v(8.17, 56.34) * mm});
            skLineSegment(sketch, "E275", {"start": v(8.17, 56.34) * mm, "end": v(8.31, 56.25) * mm});
            skLineSegment(sketch, "E276", {"start": v(8.31, 56.25) * mm, "end": v(8.69, 55.93) * mm});
            skLineSegment(sketch, "E277", {"start": v(8.69, 55.93) * mm, "end": v(9.04, 55.49) * mm});
            skLineSegment(sketch, "E278", {"start": v(9.04, 55.49) * mm, "end": v(9.26, 55.05) * mm});
            skLineSegment(sketch, "E279", {"start": v(9.26, 55.05) * mm, "end": v(9.38, 54.63) * mm});
            skLineSegment(sketch, "E280", {"start": v(9.38, 54.63) * mm, "end": v(9.42, 54.26) * mm});
            skLineSegment(sketch, "E281", {"start": v(9.42, 54.26) * mm, "end": v(9.42, 53.97) * mm});
            skLineSegment(sketch, "E282", {"start": v(9.42, 53.97) * mm, "end": v(9.4, 53.77) * mm});
            skLineSegment(sketch, "E283", {"start": v(9.4, 53.77) * mm, "end": v(9.38, 53.7) * mm});
            skLineSegment(sketch, "E284", {"start": v(9.38, 53.7) * mm, "end": v(9.52, 53.67) * mm});
            skLineSegment(sketch, "E285", {"start": v(9.52, 53.67) * mm, "end": v(9.93, 53.51) * mm});
            skLineSegment(sketch, "E286", {"start": v(9.93, 53.51) * mm, "end": v(10.45, 53.2) * mm});
            skLineSegment(sketch, "E287", {"start": v(10.45, 53.2) * mm, "end": v(10.87, 52.78) * mm});
            skLineSegment(sketch, "E288", {"start": v(10.87, 52.78) * mm, "end": v(11.12, 52.28) * mm});
            skLineSegment(sketch, "E289", {"start": v(11.12, 52.28) * mm, "end": v(11.12, 51.73) * mm});
            skLineSegment(sketch, "E290", {"start": v(11.12, 51.73) * mm, "end": v(10.8, 51.14) * mm});
            skLineSegment(sketch, "E291", {"start": v(10.8, 51.14) * mm, "end": v(10.1, 50.55) * mm});
            skLineSegment(sketch, "E292", {"start": v(10.1, 50.55) * mm, "end": v(9.24, 50.1) * mm});
            skLineSegment(sketch, "E293", {"start": v(9.24, 50.1) * mm, "end": v(8.94, 49.98) * mm});
            skLineSegment(sketch, "E294", {"start": v(5.02, 50.88) * mm, "end": v(5, 50.87) * mm});
            skLineSegment(sketch, "E295", {"start": v(5, 50.87) * mm, "end": v(4.94, 50.83) * mm});
            skLineSegment(sketch, "E296", {"start": v(4.94, 50.83) * mm, "end": v(4.82, 50.74) * mm});
            skLineSegment(sketch, "E297", {"start": v(4.82, 50.74) * mm, "end": v(4.64, 50.59) * mm});
            skLineSegment(sketch, "E298", {"start": v(4.64, 50.59) * mm, "end": v(4.37, 50.36) * mm});
            skLineSegment(sketch, "E299", {"start": v(4.37, 50.36) * mm, "end": v(4.02, 50.04) * mm});
            skLineSegment(sketch, "E300", {"start": v(4.02, 50.04) * mm, "end": v(3.56, 49.61) * mm});
            skLineSegment(sketch, "E301", {"start": v(3.56, 49.61) * mm, "end": v(3.13, 49.2) * mm});
            skLineSegment(sketch, "E302", {"start": v(3.13, 49.2) * mm, "end": v(2.99, 49.06) * mm});
            skLineSegment(sketch, "E303", {"start": v(2.99, 49.06) * mm, "end": v(2.84, 48.9) * mm});
            skLineSegment(sketch, "E304", {"start": v(2.84, 48.9) * mm, "end": v(2.5, 48.29) * mm});
            skLineSegment(sketch, "E305", {"start": v(2.5, 48.29) * mm, "end": v(2.36, 47.5) * mm});
            skLineSegment(sketch, "E306", {"start": v(2.36, 47.5) * mm, "end": v(2.5, 46.74) * mm});
            skLineSegment(sketch, "E307", {"start": v(2.5, 46.74) * mm, "end": v(2.84, 46.06) * mm});
            skLineSegment(sketch, "E308", {"start": v(2.84, 46.06) * mm, "end": v(3.33, 45.5) * mm});
            skLineSegment(sketch, "E309", {"start": v(3.33, 45.5) * mm, "end": v(3.9, 45.08) * mm});
            skLineSegment(sketch, "E310", {"start": v(3.9, 45.08) * mm, "end": v(4.5, 44.87) * mm});
            skLineSegment(sketch, "E311", {"start": v(4.5, 44.87) * mm, "end": v(4.93, 44.86) * mm});
            skLineSegment(sketch, "E312", {"start": v(4.93, 44.86) * mm, "end": v(5.06, 44.9) * mm});
            skLineSegment(sketch, "E313", {"start": v(5.06, 44.9) * mm, "end": v(5.22, 44.95) * mm});
            skLineSegment(sketch, "E314", {"start": v(5.22, 44.95) * mm, "end": v(5.7, 45.1) * mm});
            skLineSegment(sketch, "E315", {"start": v(5.7, 45.1) * mm, "end": v(6.2, 45.23) * mm});
            skLineSegment(sketch, "E316", {"start": v(6.2, 45.23) * mm, "end": v(6.6, 45.27) * mm});
            skLineSegment(sketch, "E317", {"start": v(6.6, 45.27) * mm, "end": v(6.9, 45.2) * mm});
            skLineSegment(sketch, "E318", {"start": v(6.9, 45.2) * mm, "end": v(7.17, 45.03) * mm});
            skLineSegment(sketch, "E319", {"start": v(7.17, 45.03) * mm, "end": v(7.43, 44.73) * mm});
            skLineSegment(sketch, "E320", {"start": v(7.43, 44.73) * mm, "end": v(7.72, 44.3) * mm});
            skLineSegment(sketch, "E321", {"start": v(7.72, 44.3) * mm, "end": v(8, 43.85) * mm});
            skLineSegment(sketch, "E322", {"start": v(8, 43.85) * mm, "end": v(8.08, 43.7) * mm});
            skLineSegment(sketch, "E323", {"start": v(8.08, 43.7) * mm, "end": v(7.98, 43.8) * mm});
            skLineSegment(sketch, "E324", {"start": v(7.98, 43.8) * mm, "end": v(7.66, 44.06) * mm});
            skLineSegment(sketch, "E325", {"start": v(7.66, 44.06) * mm, "end": v(7.2, 44.32) * mm});
            skLineSegment(sketch, "E326", {"start": v(7.2, 44.32) * mm, "end": v(6.75, 44.49) * mm});
            skLineSegment(sketch, "E327", {"start": v(6.75, 44.49) * mm, "end": v(6.34, 44.53) * mm});
            skLineSegment(sketch, "E328", {"start": v(6.34, 44.53) * mm, "end": v(6, 44.43) * mm});
            skLineSegment(sketch, "E329", {"start": v(6, 44.43) * mm, "end": v(5.8, 44.19) * mm});
            skLineSegment(sketch, "E330", {"start": v(5.8, 44.19) * mm, "end": v(5.73, 43.78) * mm});
            skLineSegment(sketch, "E331", {"start": v(5.73, 43.78) * mm, "end": v(5.81, 43.33) * mm});
            skLineSegment(sketch, "E332", {"start": v(5.81, 43.33) * mm, "end": v(5.86, 43.19) * mm});
            skLineSegment(sketch, "E333", {"start": v(5.86, 43.19) * mm, "end": v(5.8, 43.25) * mm});
            skLineSegment(sketch, "E334", {"start": v(5.8, 43.25) * mm, "end": v(5.58, 43.4) * mm});
            skLineSegment(sketch, "E335", {"start": v(5.58, 43.4) * mm, "end": v(5.17, 43.6) * mm});
            skLineSegment(sketch, "E336", {"start": v(5.17, 43.6) * mm, "end": v(4.65, 43.76) * mm});
            skLineSegment(sketch, "E337", {"start": v(4.65, 43.76) * mm, "end": v(4.05, 43.87) * mm});
            skLineSegment(sketch, "E338", {"start": v(4.05, 43.87) * mm, "end": v(3.42, 43.9) * mm});
            skLineSegment(sketch, "E339", {"start": v(3.42, 43.9) * mm, "end": v(2.78, 43.8) * mm});
            skLineSegment(sketch, "E340", {"start": v(2.78, 43.8) * mm, "end": v(2.16, 43.56) * mm});
            skLineSegment(sketch, "E341", {"start": v(2.16, 43.56) * mm, "end": v(1.72, 43.27) * mm});
            skLineSegment(sketch, "E342", {"start": v(1.72, 43.27) * mm, "end": v(1.6, 43.15) * mm});
            skLineSegment(sketch, "E343", {"start": v(1.6, 43.15) * mm, "end": v(1.63, 43.27) * mm});
            skLineSegment(sketch, "E344", {"start": v(1.63, 43.27) * mm, "end": v(1.81, 43.6) * mm});
            skLineSegment(sketch, "E345", {"start": v(1.81, 43.6) * mm, "end": v(2.15, 43.97) * mm});
            skLineSegment(sketch, "E346", {"start": v(2.15, 43.97) * mm, "end": v(2.52, 44.22) * mm});
            skLineSegment(sketch, "E347", {"start": v(2.52, 44.22) * mm, "end": v(2.74, 44.33) * mm});
            skLineSegment(sketch, "E348", {"start": v(2.74, 44.33) * mm, "end": v(2.81, 44.37) * mm});
            skLineSegment(sketch, "E349", {"start": v(2.81, 44.37) * mm, "end": v(2.8, 44.37) * mm});
            skLineSegment(sketch, "E350", {"start": v(2.8, 44.37) * mm, "end": v(2.76, 44.44) * mm});
            skLineSegment(sketch, "E351", {"start": v(2.76, 44.44) * mm, "end": v(2.76, 44.44) * mm});
            skLineSegment(sketch, "E352", {"start": v(2.76, 44.44) * mm, "end": v(2.73, 44.47) * mm});
            skLineSegment(sketch, "E353", {"start": v(2.73, 44.47) * mm, "end": v(2.53, 44.74) * mm});
            skLineSegment(sketch, "E354", {"start": v(2.53, 44.74) * mm, "end": v(2.51, 44.76) * mm});
            skLineSegment(sketch, "E355", {"start": v(2.51, 44.76) * mm, "end": v(2.5, 44.78) * mm});
            skLineSegment(sketch, "E356", {"start": v(2.5, 44.78) * mm, "end": v(2.35, 44.95) * mm});
            skLineSegment(sketch, "E357", {"start": v(2.35, 44.95) * mm, "end": v(2.34, 44.96) * mm});
            skLineSegment(sketch, "E358", {"start": v(2.34, 44.96) * mm, "end": v(2.2, 45.12) * mm});
            skLineSegment(sketch, "E359", {"start": v(2.2, 45.12) * mm, "end": v(1.7, 45.56) * mm});
            skLineSegment(sketch, "E360", {"start": v(1.7, 45.56) * mm, "end": v(1.1, 46) * mm});
            skLineSegment(sketch, "E361", {"start": v(1.1, 46) * mm, "end": v(0.57, 46.42) * mm});
            skLineSegment(sketch, "E362", {"start": v(0.57, 46.42) * mm, "end": v(0.26, 46.79) * mm});
            skLineSegment(sketch, "E363", {"start": v(0.26, 46.79) * mm, "end": v(0.18, 46.92) * mm});
            skLineSegment(sketch, "E364", {"start": v(0.18, 46.92) * mm, "end": v(0.03, 46.87) * mm});
            skLineSegment(sketch, "E365", {"start": v(0.03, 46.87) * mm, "end": v(-0.44, 46.75) * mm});
            skLineSegment(sketch, "E366", {"start": v(-0.44, 46.75) * mm, "end": v(-0.94, 46.67) * mm});
            skLineSegment(sketch, "E367", {"start": v(-0.94, 46.67) * mm, "end": v(-1.27, 46.66) * mm});
            skLineSegment(sketch, "E368", {"start": v(-1.27, 46.66) * mm, "end": v(-1.39, 46.67) * mm});
            skLineSegment(sketch, "E369", {"start": v(-1.39, 46.67) * mm, "end": v(-1.1, 46.8) * mm});
            skLineSegment(sketch, "E370", {"start": v(-1.1, 46.8) * mm, "end": v(-0.3, 47.3) * mm});
            skLineSegment(sketch, "E371", {"start": v(-0.3, 47.3) * mm, "end": v(0.6, 48.06) * mm});
            skLineSegment(sketch, "E372", {"start": v(0.6, 48.06) * mm, "end": v(1.51, 49.07) * mm});
            skLineSegment(sketch, "E373", {"start": v(1.51, 49.07) * mm, "end": v(2.36, 50.09) * mm});
            skLineSegment(sketch, "E374", {"start": v(2.36, 50.09) * mm, "end": v(2.64, 50.43) * mm});
            skLineSegment(sketch, "E375", {"start": v(2.64, 50.43) * mm, "end": v(2.8, 50.61) * mm});
            skLineSegment(sketch, "E376", {"start": v(2.8, 50.61) * mm, "end": v(3.32, 51.13) * mm});
            skLineSegment(sketch, "E377", {"start": v(3.32, 51.13) * mm, "end": v(4.05, 51.67) * mm});
            skLineSegment(sketch, "E378", {"start": v(4.05, 51.67) * mm, "end": v(4.82, 52.05) * mm});
            skLineSegment(sketch, "E379", {"start": v(4.82, 52.05) * mm, "end": v(5.6, 52.25) * mm});
            skLineSegment(sketch, "E380", {"start": v(5.6, 52.25) * mm, "end": v(6.39, 52.25) * mm});
            skLineSegment(sketch, "E381", {"start": v(6.39, 52.25) * mm, "end": v(7.15, 52.06) * mm});
            skLineSegment(sketch, "E382", {"start": v(7.15, 52.06) * mm, "end": v(7.9, 51.65) * mm});
            skLineSegment(sketch, "E383", {"start": v(7.9, 51.65) * mm, "end": v(8.44, 51.2) * mm});
            skLineSegment(sketch, "E384", {"start": v(8.44, 51.2) * mm, "end": v(8.6, 51.02) * mm});
            skLineSegment(sketch, "E385", {"start": v(8.6, 51.02) * mm, "end": v(8.33, 51.15) * mm});
            skLineSegment(sketch, "E386", {"start": v(8.33, 51.15) * mm, "end": v(7.5, 51.41) * mm});
            skLineSegment(sketch, "E387", {"start": v(7.5, 51.41) * mm, "end": v(6.55, 51.48) * mm});
            skLineSegment(sketch, "E388", {"start": v(6.55, 51.48) * mm, "end": v(5.73, 51.27) * mm});
            skLineSegment(sketch, "E389", {"start": v(5.73, 51.27) * mm, "end": v(5.19, 51) * mm});
            skLineSegment(sketch, "E390", {"start": v(5.19, 51) * mm, "end": v(5.02, 50.88) * mm});
            skLineSegment(sketch, "E391", {"start": v(2.77, 39.63) * mm, "end": v(2.67, 39.69) * mm});
            skLineSegment(sketch, "E392", {"start": v(2.67, 39.69) * mm, "end": v(2.35, 39.86) * mm});
            skLineSegment(sketch, "E393", {"start": v(2.35, 39.86) * mm, "end": v(1.77, 40.15) * mm});
            skLineSegment(sketch, "E394", {"start": v(1.77, 40.15) * mm, "end": v(1.07, 40.45) * mm});
            skLineSegment(sketch, "E395", {"start": v(1.07, 40.45) * mm, "end": v(0.28, 40.7) * mm});
            skLineSegment(sketch, "E396", {"start": v(0.28, 40.7) * mm, "end": v(-0.56, 40.83) * mm});
            skLineSegment(sketch, "E397", {"start": v(-0.56, 40.83) * mm, "end": v(-1.41, 40.8) * mm});
            skLineSegment(sketch, "E398", {"start": v(-1.41, 40.8) * mm, "end": v(-2.24, 40.55) * mm});
            skLineSegment(sketch, "E399", {"start": v(-2.24, 40.55) * mm, "end": v(-2.85, 40.18) * mm});
            skLineSegment(sketch, "E400", {"start": v(-2.85, 40.18) * mm, "end": v(-3.02, 40.03) * mm});
            skLineSegment(sketch, "E401", {"start": v(-3.02, 40.03) * mm, "end": v(-3, 40.13) * mm});
            skLineSegment(sketch, "E402", {"start": v(-3, 40.13) * mm, "end": v(-2.88, 40.4) * mm});
            skLineSegment(sketch, "E403", {"start": v(-2.88, 40.4) * mm, "end": v(-2.65, 40.74) * mm});
            skLineSegment(sketch, "E404", {"start": v(-2.65, 40.74) * mm, "end": v(-2.37, 41.02) * mm});
            skLineSegment(sketch, "E405", {"start": v(-2.37, 41.02) * mm, "end": v(-2.06, 41.25) * mm});
            skLineSegment(sketch, "E406", {"start": v(-2.06, 41.25) * mm, "end": v(-1.76, 41.44) * mm});
            skLineSegment(sketch, "E407", {"start": v(-1.76, 41.44) * mm, "end": v(-1.49, 41.58) * mm});
            skLineSegment(sketch, "E408", {"start": v(-1.49, 41.58) * mm, "end": v(-1.28, 41.67) * mm});
            skLineSegment(sketch, "E409", {"start": v(-1.28, 41.67) * mm, "end": v(-1.19, 41.7) * mm});
            skLineSegment(sketch, "E410", {"start": v(-1.19, 41.7) * mm, "end": v(-1.16, 41.72) * mm});
            skLineSegment(sketch, "E411", {"start": v(-1.16, 41.72) * mm, "end": v(-1.28, 41.83) * mm});
            skLineSegment(sketch, "E412", {"start": v(-1.28, 41.83) * mm, "end": v(-1.7, 42.1) * mm});
            skLineSegment(sketch, "E413", {"start": v(-1.7, 42.1) * mm, "end": v(-2.35, 42.32) * mm});
            skLineSegment(sketch, "E414", {"start": v(-2.35, 42.32) * mm, "end": v(-3.23, 42.35) * mm});
            skLineSegment(sketch, "E415", {"start": v(-3.23, 42.35) * mm, "end": v(-4.17, 42.21) * mm});
            skLineSegment(sketch, "E416", {"start": v(-4.17, 42.21) * mm, "end": v(-4.47, 42.15) * mm});
            skLineSegment(sketch, "E417", {"start": v(-4.47, 42.15) * mm, "end": v(-4.47, 42.15) * mm});
            skLineSegment(sketch, "E418", {"start": v(-4.47, 42.15) * mm, "end": v(-4.47, 42.18) * mm});
            skLineSegment(sketch, "E419", {"start": v(-4.47, 42.18) * mm, "end": v(-4.47, 42.18) * mm});
            skLineSegment(sketch, "E420", {"start": v(-4.47, 42.18) * mm, "end": v(-4.58, 42.46) * mm});
            skLineSegment(sketch, "E421", {"start": v(-4.58, 42.46) * mm, "end": v(-4.99, 43.25) * mm});
            skLineSegment(sketch, "E422", {"start": v(-4.99, 43.25) * mm, "end": v(-5.58, 44.17) * mm});
            skLineSegment(sketch, "E423", {"start": v(-5.58, 44.17) * mm, "end": v(-6.16, 44.98) * mm});
            skLineSegment(sketch, "E424", {"start": v(-6.16, 44.98) * mm, "end": v(-6.66, 45.74) * mm});
            skLineSegment(sketch, "E425", {"start": v(-6.66, 45.74) * mm, "end": v(-7, 46.48) * mm});
            skLineSegment(sketch, "E426", {"start": v(-7, 46.48) * mm, "end": v(-7.12, 47.26) * mm});
            skLineSegment(sketch, "E427", {"start": v(-7.12, 47.26) * mm, "end": v(-6.93, 48.12) * mm});
            skLineSegment(sketch, "E428", {"start": v(-6.93, 48.12) * mm, "end": v(-6.52, 48.87) * mm});
            skLineSegment(sketch, "E429", {"start": v(-6.52, 48.87) * mm, "end": v(-6.35, 49.1) * mm});
            skLineSegment(sketch, "E430", {"start": v(-6.35, 49.1) * mm, "end": v(-6.4, 48.85) * mm});
            skLineSegment(sketch, "E431", {"start": v(-6.4, 48.85) * mm, "end": v(-6.38, 48.11) * mm});
            skLineSegment(sketch, "E432", {"start": v(-6.38, 48.11) * mm, "end": v(-6.18, 47.23) * mm});
            skLineSegment(sketch, "E433", {"start": v(-6.18, 47.23) * mm, "end": v(-5.82, 46.43) * mm});
            skLineSegment(sketch, "E434", {"start": v(-5.82, 46.43) * mm, "end": v(-5.36, 45.72) * mm});
            skLineSegment(sketch, "E435", {"start": v(-5.36, 45.72) * mm, "end": v(-4.86, 45.07) * mm});
            skLineSegment(sketch, "E436", {"start": v(-4.86, 45.07) * mm, "end": v(-4.39, 44.47) * mm});
            skLineSegment(sketch, "E437", {"start": v(-4.39, 44.47) * mm, "end": v(-4.01, 43.92) * mm});
            skLineSegment(sketch, "E438", {"start": v(-4.01, 43.92) * mm, "end": v(-3.83, 43.54) * mm});
            skLineSegment(sketch, "E439", {"start": v(-3.83, 43.54) * mm, "end": v(-3.8, 43.4) * mm});
            skLineSegment(sketch, "E440", {"start": v(-3.8, 43.4) * mm, "end": v(-3.72, 43.47) * mm});
            skLineSegment(sketch, "E441", {"start": v(-3.72, 43.47) * mm, "end": v(-3.28, 43.69) * mm});
            skLineSegment(sketch, "E442", {"start": v(-3.28, 43.69) * mm, "end": v(-2.84, 43.79) * mm});
            skLineSegment(sketch, "E443", {"start": v(-2.84, 43.79) * mm, "end": v(-2.75, 43.8) * mm});
            skLineSegment(sketch, "E444", {"start": v(-2.75, 43.8) * mm, "end": v(-2.84, 43.97) * mm});
            skLineSegment(sketch, "E445", {"start": v(-2.84, 43.97) * mm, "end": v(-3.05, 44.53) * mm});
            skLineSegment(sketch, "E446", {"start": v(-3.05, 44.53) * mm, "end": v(-3.25, 45.32) * mm});
            skLineSegment(sketch, "E447", {"start": v(-3.25, 45.32) * mm, "end": v(-3.31, 46.14) * mm});
            skLineSegment(sketch, "E448", {"start": v(-3.31, 46.14) * mm, "end": v(-3.2, 46.99) * mm});
            skLineSegment(sketch, "E449", {"start": v(-3.2, 46.99) * mm, "end": v(-2.92, 47.84) * mm});
            skLineSegment(sketch, "E450", {"start": v(-2.92, 47.84) * mm, "end": v(-2.41, 48.7) * mm});
            skLineSegment(sketch, "E451", {"start": v(-2.41, 48.7) * mm, "end": v(-1.66, 49.54) * mm});
            skLineSegment(sketch, "E452", {"start": v(-1.66, 49.54) * mm, "end": v(-0.91, 50.17) * mm});
            skLineSegment(sketch, "E453", {"start": v(-0.91, 50.17) * mm, "end": v(-0.65, 50.35) * mm});
            skLineSegment(sketch, "E454", {"start": v(-0.65, 50.35) * mm, "end": v(-0.8, 50.18) * mm});
            skLineSegment(sketch, "E455", {"start": v(-0.8, 50.18) * mm, "end": v(-1.24, 49.64) * mm});
            skLineSegment(sketch, "E456", {"start": v(-1.24, 49.64) * mm, "end": v(-1.68, 48.9) * mm});
            skLineSegment(sketch, "E457", {"start": v(-1.68, 48.9) * mm, "end": v(-1.97, 48.14) * mm});
            skLineSegment(sketch, "E458", {"start": v(-1.97, 48.14) * mm, "end": v(-2.14, 47.39) * mm});
            skLineSegment(sketch, "E459", {"start": v(-2.14, 47.39) * mm, "end": v(-2.2, 46.64) * mm});
            skLineSegment(sketch, "E460", {"start": v(-2.2, 46.64) * mm, "end": v(-2.13, 45.92) * mm});
            skLineSegment(sketch, "E461", {"start": v(-2.13, 45.92) * mm, "end": v(-1.98, 45.22) * mm});
            skLineSegment(sketch, "E462", {"start": v(-1.98, 45.22) * mm, "end": v(-1.74, 44.57) * mm});
            skLineSegment(sketch, "E463", {"start": v(-1.74, 44.57) * mm, "end": v(-1.43, 43.97) * mm});
            skLineSegment(sketch, "E464", {"start": v(-1.43, 43.97) * mm, "end": v(-1.06, 43.44) * mm});
            skLineSegment(sketch, "E465", {"start": v(-1.06, 43.44) * mm, "end": v(-0.64, 42.98) * mm});
            skLineSegment(sketch, "E466", {"start": v(-0.64, 42.98) * mm, "end": v(-0.18, 42.6) * mm});
            skLineSegment(sketch, "E467", {"start": v(-0.18, 42.6) * mm, "end": v(0.3, 42.33) * mm});
            skLineSegment(sketch, "E468", {"start": v(0.3, 42.33) * mm, "end": v(0.81, 42.16) * mm});
            skLineSegment(sketch, "E469", {"start": v(0.81, 42.16) * mm, "end": v(1.32, 42.12) * mm});
            skLineSegment(sketch, "E470", {"start": v(1.32, 42.12) * mm, "end": v(1.7, 42.16) * mm});
            skLineSegment(sketch, "E471", {"start": v(1.7, 42.16) * mm, "end": v(1.82, 42.2) * mm});
            skLineSegment(sketch, "E472", {"start": v(1.82, 42.2) * mm, "end": v(2.05, 42.27) * mm});
            skLineSegment(sketch, "E473", {"start": v(2.05, 42.27) * mm, "end": v(2.76, 42.47) * mm});
            skLineSegment(sketch, "E474", {"start": v(2.76, 42.47) * mm, "end": v(3.5, 42.61) * mm});
            skLineSegment(sketch, "E475", {"start": v(3.5, 42.61) * mm, "end": v(4.1, 42.63) * mm});
            skLineSegment(sketch, "E476", {"start": v(4.1, 42.63) * mm, "end": v(4.6, 42.52) * mm});
            skLineSegment(sketch, "E477", {"start": v(4.6, 42.52) * mm, "end": v(5.05, 42.24) * mm});
            skLineSegment(sketch, "E478", {"start": v(5.05, 42.24) * mm, "end": v(5.47, 41.8) * mm});
            skLineSegment(sketch, "E479", {"start": v(5.47, 41.8) * mm, "end": v(5.92, 41.2) * mm});
            skLineSegment(sketch, "E480", {"start": v(5.92, 41.2) * mm, "end": v(6.31, 40.6) * mm});
            skLineSegment(sketch, "E481", {"start": v(6.31, 40.6) * mm, "end": v(6.44, 40.4) * mm});
            skLineSegment(sketch, "E482", {"start": v(6.44, 40.4) * mm, "end": v(6.3, 40.53) * mm});
            skLineSegment(sketch, "E483", {"start": v(6.3, 40.53) * mm, "end": v(5.82, 40.87) * mm});
            skLineSegment(sketch, "E484", {"start": v(5.82, 40.87) * mm, "end": v(5.11, 41.22) * mm});
            skLineSegment(sketch, "E485", {"start": v(5.11, 41.22) * mm, "end": v(4.39, 41.42) * mm});
            skLineSegment(sketch, "E486", {"start": v(4.39, 41.42) * mm, "end": v(3.7, 41.46) * mm});
            skLineSegment(sketch, "E487", {"start": v(3.7, 41.46) * mm, "end": v(3.14, 41.32) * mm});
            skLineSegment(sketch, "E488", {"start": v(3.14, 41.32) * mm, "end": v(2.76, 40.99) * mm});
            skLineSegment(sketch, "E489", {"start": v(2.76, 40.99) * mm, "end": v(2.61, 40.43) * mm});
            skLineSegment(sketch, "E490", {"start": v(2.61, 40.43) * mm, "end": v(2.7, 39.82) * mm});
            skLineSegment(sketch, "E491", {"start": v(2.7, 39.82) * mm, "end": v(2.77, 39.63) * mm});
            skLineSegment(sketch, "E492", {"start": v(-8.03, 41.9) * mm, "end": v(-8.07, 41.83) * mm});
            skLineSegment(sketch, "E493", {"start": v(-8.07, 41.83) * mm, "end": v(-8.22, 41.64) * mm});
            skLineSegment(sketch, "E494", {"start": v(-8.22, 41.64) * mm, "end": v(-8.52, 41.35) * mm});
            skLineSegment(sketch, "E495", {"start": v(-8.52, 41.35) * mm, "end": v(-8.9, 41.1) * mm});
            skLineSegment(sketch, "E496", {"start": v(-8.9, 41.1) * mm, "end": v(-9.2, 40.99) * mm});
            skLineSegment(sketch, "E497", {"start": v(-9.2, 40.99) * mm, "end": v(-9.31, 40.98) * mm});
            skLineSegment(sketch, "E498", {"start": v(-9.31, 40.98) * mm, "end": v(-9.27, 41.09) * mm});
            skLineSegment(sketch, "E499", {"start": v(-9.27, 41.09) * mm, "end": v(-9.14, 41.4) * mm});
            skLineSegment(sketch, "E500", {"start": v(-9.14, 41.4) * mm, "end": v(-8.95, 41.88) * mm});
            skLineSegment(sketch, "E501", {"start": v(-8.95, 41.88) * mm, "end": v(-8.72, 42.5) * mm});
            skLineSegment(sketch, "E502", {"start": v(-8.72, 42.5) * mm, "end": v(-8.47, 43.21) * mm});
            skLineSegment(sketch, "E503", {"start": v(-8.47, 43.21) * mm, "end": v(-8.22, 44) * mm});
            skLineSegment(sketch, "E504", {"start": v(-8.22, 44) * mm, "end": v(-8, 44.81) * mm});
            skLineSegment(sketch, "E505", {"start": v(-8, 44.81) * mm, "end": v(-7.85, 45.43) * mm});
            skLineSegment(sketch, "E506", {"start": v(-7.85, 45.43) * mm, "end": v(-7.81, 45.63) * mm});
            skLineSegment(sketch, "E507", {"start": v(-7.81, 45.63) * mm, "end": v(-7.8, 45.53) * mm});
            skLineSegment(sketch, "E508", {"start": v(-7.8, 45.53) * mm, "end": v(-7.78, 45.24) * mm});
            skLineSegment(sketch, "E509", {"start": v(-7.78, 45.24) * mm, "end": v(-7.75, 44.81) * mm});
            skLineSegment(sketch, "E510", {"start": v(-7.75, 44.81) * mm, "end": v(-7.73, 44.28) * mm});
            skLineSegment(sketch, "E511", {"start": v(-7.73, 44.28) * mm, "end": v(-7.74, 43.69) * mm});
            skLineSegment(sketch, "E512", {"start": v(-7.74, 43.69) * mm, "end": v(-7.79, 43.06) * mm});
            skLineSegment(sketch, "E513", {"start": v(-7.79, 43.06) * mm, "end": v(-7.88, 42.46) * mm});
            skLineSegment(sketch, "E514", {"start": v(-7.88, 42.46) * mm, "end": v(-7.98, 42.04) * mm});
            skLineSegment(sketch, "E515", {"start": v(-7.98, 42.04) * mm, "end": v(-8.03, 41.9) * mm});
            skLineSegment(sketch, "E516", {"start": v(-11.5, 40.66) * mm, "end": v(-11.58, 40.58) * mm});
            skLineSegment(sketch, "E517", {"start": v(-11.58, 40.58) * mm, "end": v(-11.89, 40.36) * mm});
            skLineSegment(sketch, "E518", {"start": v(-11.89, 40.36) * mm, "end": v(-12.31, 40.18) * mm});
            skLineSegment(sketch, "E519", {"start": v(-12.31, 40.18) * mm, "end": v(-12.74, 40.1) * mm});
            skLineSegment(sketch, "E520", {"start": v(-12.74, 40.1) * mm, "end": v(-13.14, 40.1) * mm});
            skLineSegment(sketch, "E521", {"start": v(-13.14, 40.1) * mm, "end": v(-13.5, 40.13) * mm});
            skLineSegment(sketch, "E522", {"start": v(-13.5, 40.13) * mm, "end": v(-13.77, 40.19) * mm});
            skLineSegment(sketch, "E523", {"start": v(-13.77, 40.19) * mm, "end": v(-13.96, 40.24) * mm});
            skLineSegment(sketch, "E524", {"start": v(-13.96, 40.24) * mm, "end": v(-14.03, 40.27) * mm});
            skLineSegment(sketch, "E525", {"start": v(-14.03, 40.27) * mm, "end": v(-13.72, 40.5) * mm});
            skLineSegment(sketch, "E526", {"start": v(-13.72, 40.5) * mm, "end": v(-12.83, 41.24) * mm});
            skLineSegment(sketch, "E527", {"start": v(-12.83, 41.24) * mm, "end": v(-11.75, 42.23) * mm});
            skLineSegment(sketch, "E528", {"start": v(-11.75, 42.23) * mm, "end": v(-10.8, 43.2) * mm});
            skLineSegment(sketch, "E529", {"start": v(-10.8, 43.2) * mm, "end": v(-9.97, 44.08) * mm});
            skLineSegment(sketch, "E530", {"start": v(-9.97, 44.08) * mm, "end": v(-9.31, 44.84) * mm});
            skLineSegment(sketch, "E531", {"start": v(-9.31, 44.84) * mm, "end": v(-8.82, 45.45) * mm});
            skLineSegment(sketch, "E532", {"start": v(-8.82, 45.45) * mm, "end": v(-8.52, 45.84) * mm});
            skLineSegment(sketch, "E533", {"start": v(-8.52, 45.84) * mm, "end": v(-8.4, 45.98) * mm});
            skLineSegment(sketch, "E534", {"start": v(-8.4, 45.98) * mm, "end": v(-8.4, 45.88) * mm});
            skLineSegment(sketch, "E535", {"start": v(-8.4, 45.88) * mm, "end": v(-8.48, 45.56) * mm});
            skLineSegment(sketch, "E536", {"start": v(-8.48, 45.56) * mm, "end": v(-8.72, 44.95) * mm});
            skLineSegment(sketch, "E537", {"start": v(-8.72, 44.95) * mm, "end": v(-9.1, 44.2) * mm});
            skLineSegment(sketch, "E538", {"start": v(-9.1, 44.2) * mm, "end": v(-9.56, 43.38) * mm});
            skLineSegment(sketch, "E539", {"start": v(-9.56, 43.38) * mm, "end": v(-10.07, 42.56) * mm});
            skLineSegment(sketch, "E540", {"start": v(-10.07, 42.56) * mm, "end": v(-10.6, 41.79) * mm});
            skLineSegment(sketch, "E541", {"start": v(-10.6, 41.79) * mm, "end": v(-11.08, 41.13) * mm});
            skLineSegment(sketch, "E542", {"start": v(-11.08, 41.13) * mm, "end": v(-11.38, 40.78) * mm});
            skLineSegment(sketch, "E543", {"start": v(-11.38, 40.78) * mm, "end": v(-11.5, 40.66) * mm});
            skLineSegment(sketch, "E544", {"start": v(-16.44, 41.1) * mm, "end": v(-16.57, 41.04) * mm});
            skLineSegment(sketch, "E545", {"start": v(-16.57, 41.04) * mm, "end": v(-17, 40.94) * mm});
            skLineSegment(sketch, "E546", {"start": v(-17, 40.94) * mm, "end": v(-17.58, 40.93) * mm});
            skLineSegment(sketch, "E547", {"start": v(-17.58, 40.93) * mm, "end": v(-18.15, 41.03) * mm});
            skLineSegment(sketch, "E548", {"start": v(-18.15, 41.03) * mm, "end": v(-18.67, 41.2) * mm});
            skLineSegment(sketch, "E549", {"start": v(-18.67, 41.2) * mm, "end": v(-19.12, 41.38) * mm});
            skLineSegment(sketch, "E550", {"start": v(-19.12, 41.38) * mm, "end": v(-19.47, 41.57) * mm});
            skLineSegment(sketch, "E551", {"start": v(-19.47, 41.57) * mm, "end": v(-19.7, 41.7) * mm});
            skLineSegment(sketch, "E552", {"start": v(-19.7, 41.7) * mm, "end": v(-19.8, 41.76) * mm});
            skLineSegment(sketch, "E553", {"start": v(-19.8, 41.76) * mm, "end": v(-19.14, 42.03) * mm});
            skLineSegment(sketch, "E554", {"start": v(-19.14, 42.03) * mm, "end": v(-17.2, 42.87) * mm});
            skLineSegment(sketch, "E555", {"start": v(-17.2, 42.87) * mm, "end": v(-14.95, 43.9) * mm});
            skLineSegment(sketch, "E556", {"start": v(-14.95, 43.9) * mm, "end": v(-13.04, 44.8) * mm});
            skLineSegment(sketch, "E557", {"start": v(-13.04, 44.8) * mm, "end": v(-11.48, 45.6) * mm});
            skLineSegment(sketch, "E558", {"start": v(-11.48, 45.6) * mm, "end": v(-10.27, 46.25) * mm});
            skLineSegment(sketch, "E559", {"start": v(-10.27, 46.25) * mm, "end": v(-9.4, 46.73) * mm});
            skLineSegment(sketch, "E560", {"start": v(-9.4, 46.73) * mm, "end": v(-8.89, 47.04) * mm});
            skLineSegment(sketch, "E561", {"start": v(-8.89, 47.04) * mm, "end": v(-8.71, 47.14) * mm});
            skLineSegment(sketch, "E562", {"start": v(-8.71, 47.14) * mm, "end": v(-8.75, 46.97) * mm});
            skLineSegment(sketch, "E563", {"start": v(-8.75, 46.97) * mm, "end": v(-9.07, 46.5) * mm});
            skLineSegment(sketch, "E564", {"start": v(-9.07, 46.5) * mm, "end": v(-9.82, 45.7) * mm});
            skLineSegment(sketch, "E565", {"start": v(-9.82, 45.7) * mm, "end": v(-10.87, 44.79) * mm});
            skLineSegment(sketch, "E566", {"start": v(-10.87, 44.79) * mm, "end": v(-12.09, 43.85) * mm});
            skLineSegment(sketch, "E567", {"start": v(-12.09, 43.85) * mm, "end": v(-13.37, 42.94) * mm});
            skLineSegment(sketch, "E568", {"start": v(-13.37, 42.94) * mm, "end": v(-14.6, 42.14) * mm});
            skLineSegment(sketch, "E569", {"start": v(-14.6, 42.14) * mm, "end": v(-15.66, 41.5) * mm});
            skLineSegment(sketch, "E570", {"start": v(-15.66, 41.5) * mm, "end": v(-16.24, 41.18) * mm});
            skLineSegment(sketch, "E571", {"start": v(-16.24, 41.18) * mm, "end": v(-16.44, 41.1) * mm});
            skLineSegment(sketch, "E572", {"start": v(-21.95, 43.47) * mm, "end": v(-22.11, 43.46) * mm});
            skLineSegment(sketch, "E573", {"start": v(-22.11, 43.46) * mm, "end": v(-22.6, 43.51) * mm});
            skLineSegment(sketch, "E574", {"start": v(-22.6, 43.51) * mm, "end": v(-23.2, 43.7) * mm});
            skLineSegment(sketch, "E575", {"start": v(-23.2, 43.7) * mm, "end": v(-23.7, 43.99) * mm});
            skLineSegment(sketch, "E576", {"start": v(-23.7, 43.99) * mm, "end": v(-24.14, 44.33) * mm});
            skLineSegment(sketch, "E577", {"start": v(-24.14, 44.33) * mm, "end": v(-24.49, 44.67) * mm});
            skLineSegment(sketch, "E578", {"start": v(-24.49, 44.67) * mm, "end": v(-24.74, 44.98) * mm});
            skLineSegment(sketch, "E579", {"start": v(-24.74, 44.98) * mm, "end": v(-24.9, 45.2) * mm});
            skLineSegment(sketch, "E580", {"start": v(-24.9, 45.2) * mm, "end": v(-24.95, 45.28) * mm});
            skLineSegment(sketch, "E581", {"start": v(-24.95, 45.28) * mm, "end": v(-24.7, 45.31) * mm});
            skLineSegment(sketch, "E582", {"start": v(-24.7, 45.31) * mm, "end": v(-23.97, 45.43) * mm});
            skLineSegment(sketch, "E583", {"start": v(-23.97, 45.43) * mm, "end": v(-22.87, 45.63) * mm});
            skLineSegment(sketch, "E584", {"start": v(-22.87, 45.63) * mm, "end": v(-21.66, 45.87) * mm});
            skLineSegment(sketch, "E585", {"start": v(-21.66, 45.87) * mm, "end": v(-20.38, 46.14) * mm});
            skLineSegment(sketch, "E586", {"start": v(-20.38, 46.14) * mm, "end": v(-19.05, 46.43) * mm});
            skLineSegment(sketch, "E587", {"start": v(-19.05, 46.43) * mm, "end": v(-17.7, 46.74) * mm});
            skLineSegment(sketch, "E588", {"start": v(-17.7, 46.74) * mm, "end": v(-16.34, 47.06) * mm});
            skLineSegment(sketch, "E589", {"start": v(-16.34, 47.06) * mm, "end": v(-15.03, 47.38) * mm});
            skLineSegment(sketch, "E590", {"start": v(-15.03, 47.38) * mm, "end": v(-13.76, 47.69) * mm});
            skLineSegment(sketch, "E591", {"start": v(-13.76, 47.69) * mm, "end": v(-12.59, 47.98) * mm});
            skLineSegment(sketch, "E592", {"start": v(-12.59, 47.98) * mm, "end": v(-11.52, 48.25) * mm});
            skLineSegment(sketch, "E593", {"start": v(-11.52, 48.25) * mm, "end": v(-10.58, 48.5) * mm});
            skLineSegment(sketch, "E594", {"start": v(-10.58, 48.5) * mm, "end": v(-9.81, 48.7) * mm});
            skLineSegment(sketch, "E595", {"start": v(-9.81, 48.7) * mm, "end": v(-9.23, 48.84) * mm});
            skLineSegment(sketch, "E596", {"start": v(-9.23, 48.84) * mm, "end": v(-8.86, 48.94) * mm});
            skLineSegment(sketch, "E597", {"start": v(-8.86, 48.94) * mm, "end": v(-8.73, 48.98) * mm});
            skLineSegment(sketch, "E598", {"start": v(-8.73, 48.98) * mm, "end": v(-8.8, 48.88) * mm});
            skLineSegment(sketch, "E599", {"start": v(-8.8, 48.88) * mm, "end": v(-9.06, 48.62) * mm});
            skLineSegment(sketch, "E600", {"start": v(-9.06, 48.62) * mm, "end": v(-9.57, 48.22) * mm});
            skLineSegment(sketch, "E601", {"start": v(-9.57, 48.22) * mm, "end": v(-10.25, 47.8) * mm});
            skLineSegment(sketch, "E602", {"start": v(-10.25, 47.8) * mm, "end": v(-11.06, 47.36) * mm});
            skLineSegment(sketch, "E603", {"start": v(-11.06, 47.36) * mm, "end": v(-11.98, 46.92) * mm});
            skLineSegment(sketch, "E604", {"start": v(-11.98, 46.92) * mm, "end": v(-12.98, 46.47) * mm});
            skLineSegment(sketch, "E605", {"start": v(-12.98, 46.47) * mm, "end": v(-14.04, 46.02) * mm});
            skLineSegment(sketch, "E606", {"start": v(-14.04, 46.02) * mm, "end": v(-15.13, 45.59) * mm});
            skLineSegment(sketch, "E607", {"start": v(-15.13, 45.59) * mm, "end": v(-16.23, 45.17) * mm});
            skLineSegment(sketch, "E608", {"start": v(-16.23, 45.17) * mm, "end": v(-17.31, 44.79) * mm});
            skLineSegment(sketch, "E609", {"start": v(-17.31, 44.79) * mm, "end": v(-18.35, 44.43) * mm});
            skLineSegment(sketch, "E610", {"start": v(-18.35, 44.43) * mm, "end": v(-19.3, 44.13) * mm});
            skLineSegment(sketch, "E611", {"start": v(-19.3, 44.13) * mm, "end": v(-20.18, 43.87) * mm});
            skLineSegment(sketch, "E612", {"start": v(-20.18, 43.87) * mm, "end": v(-20.93, 43.67) * mm});
            skLineSegment(sketch, "E613", {"start": v(-20.93, 43.67) * mm, "end": v(-21.53, 43.53) * mm});
            skLineSegment(sketch, "E614", {"start": v(-21.53, 43.53) * mm, "end": v(-21.85, 43.48) * mm});
            skLineSegment(sketch, "E615", {"start": v(-21.85, 43.48) * mm, "end": v(-21.95, 43.47) * mm});
            skLineSegment(sketch, "E616", {"start": v(-23.3, 56.4) * mm, "end": v(-23.59, 56.6) * mm});
            skLineSegment(sketch, "E617", {"start": v(-23.59, 56.6) * mm, "end": v(-24.54, 57.11) * mm});
            skLineSegment(sketch, "E618", {"start": v(-24.54, 57.11) * mm, "end": v(-25.92, 57.63) * mm});
            skLineSegment(sketch, "E619", {"start": v(-25.92, 57.63) * mm, "end": v(-27.34, 57.98) * mm});
            skLineSegment(sketch, "E620", {"start": v(-27.34, 57.98) * mm, "end": v(-28.72, 58.2) * mm});
            skLineSegment(sketch, "E621", {"start": v(-28.72, 58.2) * mm, "end": v(-29.95, 58.32) * mm});
            skLineSegment(sketch, "E622", {"start": v(-29.95, 58.32) * mm, "end": v(-30.95, 58.37) * mm});
            skLineSegment(sketch, "E623", {"start": v(-30.95, 58.37) * mm, "end": v(-31.61, 58.37) * mm});
            skLineSegment(sketch, "E624", {"start": v(-31.61, 58.37) * mm, "end": v(-31.85, 58.37) * mm});
            skLineSegment(sketch, "E625", {"start": v(-31.85, 58.37) * mm, "end": v(-31.47, 58.53) * mm});
            skLineSegment(sketch, "E626", {"start": v(-31.47, 58.53) * mm, "end": v(-30.27, 58.88) * mm});
            skLineSegment(sketch, "E627", {"start": v(-30.27, 58.88) * mm, "end": v(-28.65, 59.13) * mm});
            skLineSegment(sketch, "E628", {"start": v(-28.65, 59.13) * mm, "end": v(-27.02, 59.13) * mm});
            skLineSegment(sketch, "E629", {"start": v(-27.02, 59.13) * mm, "end": v(-25.41, 58.9) * mm});
            skLineSegment(sketch, "E630", {"start": v(-25.41, 58.9) * mm, "end": v(-23.85, 58.44) * mm});
            skLineSegment(sketch, "E631", {"start": v(-23.85, 58.44) * mm, "end": v(-22.37, 57.77) * mm});
            skLineSegment(sketch, "E632", {"start": v(-22.37, 57.77) * mm, "end": v(-21, 56.9) * mm});
            skLineSegment(sketch, "E633", {"start": v(-21, 56.9) * mm, "end": v(-20.04, 56.1) * mm});
            skLineSegment(sketch, "E634", {"start": v(-20.04, 56.1) * mm, "end": v(-19.76, 55.82) * mm});
            skLineSegment(sketch, "E635", {"start": v(-19.76, 55.82) * mm, "end": v(-19.2, 55.27) * mm});
            skLineSegment(sketch, "E636", {"start": v(-19.2, 55.27) * mm, "end": v(-17.47, 53.71) * mm});
            skLineSegment(sketch, "E637", {"start": v(-17.47, 53.71) * mm, "end": v(-15.36, 52.17) * mm});
            skLineSegment(sketch, "E638", {"start": v(-15.36, 52.17) * mm, "end": v(-13.47, 51.22) * mm});
            skLineSegment(sketch, "E639", {"start": v(-13.47, 51.22) * mm, "end": v(-12.25, 50.9) * mm});
            skLineSegment(sketch, "E640", {"start": v(-12.25, 50.9) * mm, "end": v(-11.85, 50.9) * mm});
            skLineSegment(sketch, "E641", {"start": v(-11.85, 50.9) * mm, "end": v(-11.54, 50.9) * mm});
            skLineSegment(sketch, "E642", {"start": v(-11.54, 50.9) * mm, "end": v(-10.62, 50.96) * mm});
            skLineSegment(sketch, "E643", {"start": v(-10.62, 50.96) * mm, "end": v(-9.8, 51.1) * mm});
            skLineSegment(sketch, "E644", {"start": v(-9.8, 51.1) * mm, "end": v(-9.36, 51.24) * mm});
            skLineSegment(sketch, "E645", {"start": v(-9.36, 51.24) * mm, "end": v(-9.22, 51.3) * mm});
            skLineSegment(sketch, "E646", {"start": v(-9.22, 51.3) * mm, "end": v(-9.35, 51.14) * mm});
            skLineSegment(sketch, "E647", {"start": v(-9.35, 51.14) * mm, "end": v(-9.78, 50.77) * mm});
            skLineSegment(sketch, "E648", {"start": v(-9.78, 50.77) * mm, "end": v(-10.6, 50.37) * mm});
            skLineSegment(sketch, "E649", {"start": v(-10.6, 50.37) * mm, "end": v(-11.55, 50.13) * mm});
            skLineSegment(sketch, "E650", {"start": v(-11.55, 50.13) * mm, "end": v(-11.88, 50.1) * mm});
            skLineSegment(sketch, "E651", {"start": v(-11.88, 50.1) * mm, "end": v(-12.3, 50.07) * mm});
            skLineSegment(sketch, "E652", {"start": v(-12.3, 50.07) * mm, "end": v(-13.57, 50.17) * mm});
            skLineSegment(sketch, "E653", {"start": v(-13.57, 50.17) * mm, "end": v(-15.19, 50.62) * mm});
            skLineSegment(sketch, "E654", {"start": v(-15.19, 50.62) * mm, "end": v(-16.73, 51.36) * mm});
            skLineSegment(sketch, "E655", {"start": v(-16.73, 51.36) * mm, "end": v(-18.2, 52.3) * mm});
            skLineSegment(sketch, "E656", {"start": v(-18.2, 52.3) * mm, "end": v(-19.58, 53.36) * mm});
            skLineSegment(sketch, "E657", {"start": v(-19.58, 53.36) * mm, "end": v(-20.9, 54.46) * mm});
            skLineSegment(sketch, "E658", {"start": v(-20.9, 54.46) * mm, "end": v(-22.14, 55.5) * mm});
            skLineSegment(sketch, "E659", {"start": v(-22.14, 55.5) * mm, "end": v(-23, 56.19) * mm});
            skLineSegment(sketch, "E660", {"start": v(-23, 56.19) * mm, "end": v(-23.3, 56.4) * mm});
            skLineSegment(sketch, "E661", {"start": v(-38.58, 59.53) * mm, "end": v(-38.75, 59.55) * mm});
            skLineSegment(sketch, "E662", {"start": v(-38.75, 59.55) * mm, "end": v(-39.26, 59.7) * mm});
            skLineSegment(sketch, "E663", {"start": v(-39.26, 59.7) * mm, "end": v(-39.91, 60.05) * mm});
            skLineSegment(sketch, "E664", {"start": v(-39.91, 60.05) * mm, "end": v(-40.53, 60.5) * mm});
            skLineSegment(sketch, "E665", {"start": v(-40.53, 60.5) * mm, "end": v(-41.08, 61) * mm});
            skLineSegment(sketch, "E666", {"start": v(-41.08, 61) * mm, "end": v(-41.54, 61.51) * mm});
            skLineSegment(sketch, "E667", {"start": v(-41.54, 61.51) * mm, "end": v(-41.9, 61.94) * mm});
            skLineSegment(sketch, "E668", {"start": v(-41.9, 61.94) * mm, "end": v(-42.13, 62.25) * mm});
            skLineSegment(sketch, "E669", {"start": v(-42.13, 62.25) * mm, "end": v(-42.22, 62.36) * mm});
            skLineSegment(sketch, "E670", {"start": v(-42.22, 62.36) * mm, "end": v(-41.98, 62.3) * mm});
            skLineSegment(sketch, "E671", {"start": v(-41.98, 62.3) * mm, "end": v(-41.27, 62.23) * mm});
            skLineSegment(sketch, "E672", {"start": v(-41.27, 62.23) * mm, "end": v(-39.8, 62.15) * mm});
            skLineSegment(sketch, "E673", {"start": v(-39.8, 62.15) * mm, "end": v(-37.94, 62.16) * mm});
            skLineSegment(sketch, "E674", {"start": v(-37.94, 62.16) * mm, "end": v(-35.8, 62.28) * mm});
            skLineSegment(sketch, "E675", {"start": v(-35.8, 62.28) * mm, "end": v(-33.5, 62.53) * mm});
            skLineSegment(sketch, "E676", {"start": v(-33.5, 62.53) * mm, "end": v(-31.15, 62.95) * mm});
            skLineSegment(sketch, "E677", {"start": v(-31.15, 62.95) * mm, "end": v(-28.9, 63.56) * mm});
            skLineSegment(sketch, "E678", {"start": v(-28.9, 63.56) * mm, "end": v(-27.35, 64.15) * mm});
            skLineSegment(sketch, "E679", {"start": v(-27.35, 64.15) * mm, "end": v(-26.85, 64.39) * mm});
            skLineSegment(sketch, "E680", {"start": v(-26.85, 64.39) * mm, "end": v(-27.1, 64.16) * mm});
            skLineSegment(sketch, "E681", {"start": v(-27.1, 64.16) * mm, "end": v(-27.77, 63.55) * mm});
            skLineSegment(sketch, "E682", {"start": v(-27.77, 63.55) * mm, "end": v(-28.85, 62.7) * mm});
            skLineSegment(sketch, "E683", {"start": v(-28.85, 62.7) * mm, "end": v(-30.28, 61.75) * mm});
            skLineSegment(sketch, "E684", {"start": v(-30.28, 61.75) * mm, "end": v(-32.02, 60.82) * mm});
            skLineSegment(sketch, "E685", {"start": v(-32.02, 60.82) * mm, "end": v(-34, 60.05) * mm});
            skLineSegment(sketch, "E686", {"start": v(-34, 60.05) * mm, "end": v(-36.21, 59.58) * mm});
            skLineSegment(sketch, "E687", {"start": v(-36.21, 59.58) * mm, "end": v(-38, 59.48) * mm});
            skLineSegment(sketch, "E688", {"start": v(-38, 59.48) * mm, "end": v(-38.58, 59.53) * mm});
            skLineSegment(sketch, "E689", {"start": v(-43.78, 66.22) * mm, "end": v(-44, 66.27) * mm});
            skLineSegment(sketch, "E690", {"start": v(-44, 66.27) * mm, "end": v(-44.6, 66.57) * mm});
            skLineSegment(sketch, "E691", {"start": v(-44.6, 66.57) * mm, "end": v(-45.33, 67.18) * mm});
            skLineSegment(sketch, "E692", {"start": v(-45.33, 67.18) * mm, "end": v(-45.97, 67.95) * mm});
            skLineSegment(sketch, "E693", {"start": v(-45.97, 67.95) * mm, "end": v(-46.5, 68.8) * mm});
            skLineSegment(sketch, "E694", {"start": v(-46.5, 68.8) * mm, "end": v(-46.93, 69.61) * mm});
            skLineSegment(sketch, "E695", {"start": v(-46.93, 69.61) * mm, "end": v(-47.25, 70.32) * mm});
            skLineSegment(sketch, "E696", {"start": v(-47.25, 70.32) * mm, "end": v(-47.44, 70.8) * mm});
            skLineSegment(sketch, "E697", {"start": v(-47.44, 70.8) * mm, "end": v(-47.5, 70.99) * mm});
            skLineSegment(sketch, "E698", {"start": v(-47.5, 70.99) * mm, "end": v(-47.35, 70.93) * mm});
            skLineSegment(sketch, "E699", {"start": v(-47.35, 70.93) * mm, "end": v(-46.87, 70.77) * mm});
            skLineSegment(sketch, "E700", {"start": v(-46.87, 70.77) * mm, "end": v(-46.04, 70.51) * mm});
            skLineSegment(sketch, "E701", {"start": v(-46.04, 70.51) * mm, "end": v(-45.04, 70.24) * mm});
            skLineSegment(sketch, "E702", {"start": v(-45.04, 70.24) * mm, "end": v(-43.88, 69.95) * mm});
            skLineSegment(sketch, "E703", {"start": v(-43.88, 69.95) * mm, "end": v(-42.6, 69.66) * mm});
            skLineSegment(sketch, "E704", {"start": v(-42.6, 69.66) * mm, "end": v(-41.18, 69.38) * mm});
            skLineSegment(sketch, "E705", {"start": v(-41.18, 69.38) * mm, "end": v(-39.67, 69.1) * mm});
            skLineSegment(sketch, "E706", {"start": v(-39.67, 69.1) * mm, "end": v(-38.09, 68.86) * mm});
            skLineSegment(sketch, "E707", {"start": v(-38.09, 68.86) * mm, "end": v(-36.43, 68.64) * mm});
            skLineSegment(sketch, "E708", {"start": v(-36.43, 68.64) * mm, "end": v(-34.74, 68.47) * mm});
            skLineSegment(sketch, "E709", {"start": v(-34.74, 68.47) * mm, "end": v(-33.01, 68.35) * mm});
            skLineSegment(sketch, "E710", {"start": v(-33.01, 68.35) * mm, "end": v(-31.28, 68.28) * mm});
            skLineSegment(sketch, "E711", {"start": v(-31.28, 68.28) * mm, "end": v(-29.56, 68.28) * mm});
            skLineSegment(sketch, "E712", {"start": v(-29.56, 68.28) * mm, "end": v(-27.87, 68.36) * mm});
            skLineSegment(sketch, "E713", {"start": v(-27.87, 68.36) * mm, "end": v(-26.22, 68.53) * mm});
            skLineSegment(sketch, "E714", {"start": v(-26.22, 68.53) * mm, "end": v(-25.03, 68.7) * mm});
            skLineSegment(sketch, "E715", {"start": v(-25.03, 68.7) * mm, "end": v(-24.64, 68.78) * mm});
            skLineSegment(sketch, "E716", {"start": v(-24.64, 68.78) * mm, "end": v(-24.74, 68.73) * mm});
            skLineSegment(sketch, "E717", {"start": v(-24.74, 68.73) * mm, "end": v(-25.02, 68.58) * mm});
            skLineSegment(sketch, "E718", {"start": v(-25.02, 68.58) * mm, "end": v(-25.5, 68.35) * mm});
            skLineSegment(sketch, "E719", {"start": v(-25.5, 68.35) * mm, "end": v(-26.13, 68.05) * mm});
            skLineSegment(sketch, "E720", {"start": v(-26.13, 68.05) * mm, "end": v(-26.93, 67.72) * mm});
            skLineSegment(sketch, "E721", {"start": v(-26.93, 67.72) * mm, "end": v(-27.88, 67.36) * mm});
            skLineSegment(sketch, "E722", {"start": v(-27.88, 67.36) * mm, "end": v(-28.98, 66.99) * mm});
            skLineSegment(sketch, "E723", {"start": v(-28.98, 66.99) * mm, "end": v(-30.2, 66.63) * mm});
            skLineSegment(sketch, "E724", {"start": v(-30.2, 66.63) * mm, "end": v(-31.56, 66.3) * mm});
            skLineSegment(sketch, "E725", {"start": v(-31.56, 66.3) * mm, "end": v(-33.03, 66) * mm});
            skLineSegment(sketch, "E726", {"start": v(-33.03, 66) * mm, "end": v(-34.61, 65.78) * mm});
            skLineSegment(sketch, "E727", {"start": v(-34.61, 65.78) * mm, "end": v(-36.29, 65.64) * mm});
            skLineSegment(sketch, "E728", {"start": v(-36.29, 65.64) * mm, "end": v(-38.05, 65.6) * mm});
            skLineSegment(sketch, "E729", {"start": v(-38.05, 65.6) * mm, "end": v(-39.9, 65.66) * mm});
            skLineSegment(sketch, "E730", {"start": v(-39.9, 65.66) * mm, "end": v(-41.8, 65.87) * mm});
            skLineSegment(sketch, "E731", {"start": v(-41.8, 65.87) * mm, "end": v(-43.3, 66.11) * mm});
            skLineSegment(sketch, "E732", {"start": v(-43.3, 66.11) * mm, "end": v(-43.78, 66.22) * mm});
            skLineSegment(sketch, "E733", {"start": v(-41.97, 73.88) * mm, "end": v(-42.18, 73.98) * mm});
            skLineSegment(sketch, "E734", {"start": v(-42.18, 73.98) * mm, "end": v(-42.73, 74.4) * mm});
            skLineSegment(sketch, "E735", {"start": v(-42.73, 74.4) * mm, "end": v(-43.38, 75.13) * mm});
            skLineSegment(sketch, "E736", {"start": v(-43.38, 75.13) * mm, "end": v(-43.93, 76) * mm});
            skLineSegment(sketch, "E737", {"start": v(-43.93, 76) * mm, "end": v(-44.37, 76.9) * mm});
            skLineSegment(sketch, "E738", {"start": v(-44.37, 76.9) * mm, "end": v(-44.7, 77.76) * mm});
            skLineSegment(sketch, "E739", {"start": v(-44.7, 77.76) * mm, "end": v(-44.94, 78.48) * mm});
            skLineSegment(sketch, "E740", {"start": v(-44.94, 78.48) * mm, "end": v(-45.08, 78.98) * mm});
            skLineSegment(sketch, "E741", {"start": v(-45.08, 78.98) * mm, "end": v(-45.13, 79.17) * mm});
            skLineSegment(sketch, "E742", {"start": v(-45.13, 79.17) * mm, "end": v(-44.8, 78.96) * mm});
            skLineSegment(sketch, "E743", {"start": v(-44.8, 78.96) * mm, "end": v(-43.77, 78.4) * mm});
            skLineSegment(sketch, "E744", {"start": v(-43.77, 78.4) * mm, "end": v(-41.8, 77.47) * mm});
            skLineSegment(sketch, "E745", {"start": v(-41.8, 77.47) * mm, "end": v(-39.34, 76.43) * mm});
            skLineSegment(sketch, "E746", {"start": v(-39.34, 76.43) * mm, "end": v(-36.5, 75.37) * mm});
            skLineSegment(sketch, "E747", {"start": v(-36.5, 75.37) * mm, "end": v(-33.42, 74.37) * mm});
            skLineSegment(sketch, "E748", {"start": v(-33.42, 74.37) * mm, "end": v(-30.19, 73.5) * mm});
            skLineSegment(sketch, "E749", {"start": v(-30.19, 73.5) * mm, "end": v(-26.94, 72.86) * mm});
            skLineSegment(sketch, "E750", {"start": v(-26.94, 72.86) * mm, "end": v(-24.57, 72.56) * mm});
            skLineSegment(sketch, "E751", {"start": v(-24.57, 72.56) * mm, "end": v(-23.78, 72.51) * mm});
            skLineSegment(sketch, "E752", {"start": v(-23.78, 72.51) * mm, "end": v(-23.88, 72.48) * mm});
            skLineSegment(sketch, "E753", {"start": v(-23.88, 72.48) * mm, "end": v(-24.15, 72.38) * mm});
            skLineSegment(sketch, "E754", {"start": v(-24.15, 72.38) * mm, "end": v(-24.6, 72.24) * mm});
            skLineSegment(sketch, "E755", {"start": v(-24.6, 72.24) * mm, "end": v(-25.2, 72.08) * mm});
            skLineSegment(sketch, "E756", {"start": v(-25.2, 72.08) * mm, "end": v(-25.97, 71.9) * mm});
            skLineSegment(sketch, "E757", {"start": v(-25.97, 71.9) * mm, "end": v(-26.87, 71.73) * mm});
            skLineSegment(sketch, "E758", {"start": v(-26.87, 71.73) * mm, "end": v(-27.92, 71.58) * mm});
            skLineSegment(sketch, "E759", {"start": v(-27.92, 71.58) * mm, "end": v(-29.09, 71.46) * mm});
            skLineSegment(sketch, "E760", {"start": v(-29.09, 71.46) * mm, "end": v(-30.38, 71.4) * mm});
            skLineSegment(sketch, "E761", {"start": v(-30.38, 71.4) * mm, "end": v(-31.78, 71.42) * mm});
            skLineSegment(sketch, "E762", {"start": v(-31.78, 71.42) * mm, "end": v(-33.28, 71.51) * mm});
            skLineSegment(sketch, "E763", {"start": v(-33.28, 71.51) * mm, "end": v(-34.87, 71.72) * mm});
            skLineSegment(sketch, "E764", {"start": v(-34.87, 71.72) * mm, "end": v(-36.54, 72.04) * mm});
            skLineSegment(sketch, "E765", {"start": v(-36.54, 72.04) * mm, "end": v(-38.29, 72.5) * mm});
            skLineSegment(sketch, "E766", {"start": v(-38.29, 72.5) * mm, "end": v(-40.1, 73.1) * mm});
            skLineSegment(sketch, "E767", {"start": v(-40.1, 73.1) * mm, "end": v(-41.51, 73.67) * mm});
            skLineSegment(sketch, "E768", {"start": v(-41.51, 73.67) * mm, "end": v(-41.97, 73.88) * mm});
            skLineSegment(sketch, "E769", {"start": v(1.73, 64.95) * mm, "end": v(1.92, 65.21) * mm});
            skLineSegment(sketch, "E770", {"start": v(1.92, 65.21) * mm, "end": v(2.47, 66) * mm});
            skLineSegment(sketch, "E771", {"start": v(2.47, 66) * mm, "end": v(3.22, 67.1) * mm});
            skLineSegment(sketch, "E772", {"start": v(3.22, 67.1) * mm, "end": v(3.97, 68.19) * mm});
            skLineSegment(sketch, "E773", {"start": v(3.97, 68.19) * mm, "end": v(4.7, 69.24) * mm});
            skLineSegment(sketch, "E774", {"start": v(4.7, 69.24) * mm, "end": v(5.37, 70.22) * mm});
            skLineSegment(sketch, "E775", {"start": v(5.37, 70.22) * mm, "end": v(5.96, 71.1) * mm});
            skLineSegment(sketch, "E776", {"start": v(5.96, 71.1) * mm, "end": v(6.46, 71.84) * mm});
            skLineSegment(sketch, "E777", {"start": v(6.46, 71.84) * mm, "end": v(6.73, 72.27) * mm});
            skLineSegment(sketch, "E778", {"start": v(6.73, 72.27) * mm, "end": v(6.82, 72.4) * mm});
            skLineSegment(sketch, "E779", {"start": v(6.82, 72.4) * mm, "end": v(6.83, 72.42) * mm});
            skLineSegment(sketch, "E780", {"start": v(6.83, 72.42) * mm, "end": v(6.93, 72.6) * mm});
            skLineSegment(sketch, "E781", {"start": v(6.93, 72.6) * mm, "end": v(6.94, 72.62) * mm});
            skLineSegment(sketch, "E782", {"start": v(6.94, 72.62) * mm, "end": v(6.97, 72.67) * mm});
            skLineSegment(sketch, "E783", {"start": v(6.97, 72.67) * mm, "end": v(7.34, 73.15) * mm});
            skLineSegment(sketch, "E784", {"start": v(7.34, 73.15) * mm, "end": v(7.38, 73.2) * mm});
            skLineSegment(sketch, "E785", {"start": v(7.38, 73.2) * mm, "end": v(7.38, 73.2) * mm});
            skLineSegment(sketch, "E786", {"start": v(7.38, 73.2) * mm, "end": v(7.4, 73.23) * mm});
            skLineSegment(sketch, "E787", {"start": v(7.4, 73.23) * mm, "end": v(7.41, 73.24) * mm});
            skLineSegment(sketch, "E788", {"start": v(7.41, 73.24) * mm, "end": v(7.42, 73.25) * mm});
            skLineSegment(sketch, "E789", {"start": v(7.42, 73.25) * mm, "end": v(7.5, 73.32) * mm});
            skLineSegment(sketch, "E790", {"start": v(7.5, 73.32) * mm, "end": v(7.5, 73.33) * mm});
            skLineSegment(sketch, "E791", {"start": v(7.5, 73.33) * mm, "end": v(7.5, 73.34) * mm});
            skLineSegment(sketch, "E792", {"start": v(7.5, 73.34) * mm, "end": v(7.64, 73.48) * mm});
            skLineSegment(sketch, "E793", {"start": v(7.64, 73.48) * mm, "end": v(7.66, 73.5) * mm});
            skLineSegment(sketch, "E794", {"start": v(7.66, 73.5) * mm, "end": v(7.66, 73.5) * mm});
            skLineSegment(sketch, "E795", {"start": v(7.66, 73.5) * mm, "end": v(7.68, 73.51) * mm});
            skLineSegment(sketch, "E796", {"start": v(7.68, 73.51) * mm, "end": v(7.68, 73.52) * mm});
            skLineSegment(sketch, "E797", {"start": v(7.68, 73.52) * mm, "end": v(7.71, 73.54) * mm});
            skLineSegment(sketch, "E798", {"start": v(7.71, 73.54) * mm, "end": v(8.03, 73.83) * mm});
            skLineSegment(sketch, "E799", {"start": v(8.03, 73.83) * mm, "end": v(8.06, 73.86) * mm});
            skLineSegment(sketch, "E800", {"start": v(8.06, 73.86) * mm, "end": v(8.07, 73.86) * mm});
            skLineSegment(sketch, "E801", {"start": v(8.07, 73.86) * mm, "end": v(8.14, 73.92) * mm});
            skLineSegment(sketch, "E802", {"start": v(8.14, 73.92) * mm, "end": v(8.15, 73.92) * mm});
            skLineSegment(sketch, "E803", {"start": v(8.15, 73.92) * mm, "end": v(8.16, 73.93) * mm});
            skLineSegment(sketch, "E804", {"start": v(8.16, 73.93) * mm, "end": v(8.24, 74) * mm});
            skLineSegment(sketch, "E805", {"start": v(8.24, 74) * mm, "end": v(8.25, 74) * mm});
            skLineSegment(sketch, "E806", {"start": v(8.25, 74) * mm, "end": v(8.48, 74.18) * mm});
            skLineSegment(sketch, "E807", {"start": v(8.48, 74.18) * mm, "end": v(9.24, 74.62) * mm});
            skLineSegment(sketch, "E808", {"start": v(9.24, 74.62) * mm, "end": v(10.53, 75.2) * mm});
            skLineSegment(sketch, "E809", {"start": v(10.53, 75.2) * mm, "end": v(12.17, 75.75) * mm});
            skLineSegment(sketch, "E810", {"start": v(12.17, 75.75) * mm, "end": v(13.7, 76.18) * mm});
            skLineSegment(sketch, "E811", {"start": v(13.7, 76.18) * mm, "end": v(14.2, 76.32) * mm});
            skLineSegment(sketch, "E812", {"start": v(14.2, 76.32) * mm, "end": v(14.9, 76.5) * mm});
            skLineSegment(sketch, "E813", {"start": v(14.9, 76.5) * mm, "end": v(16.98, 77.11) * mm});
            skLineSegment(sketch, "E814", {"start": v(16.98, 77.11) * mm, "end": v(19.05, 77.8) * mm});
            skLineSegment(sketch, "E815", {"start": v(19.05, 77.8) * mm, "end": v(20.4, 78.33) * mm});
            skLineSegment(sketch, "E816", {"start": v(20.4, 78.33) * mm, "end": v(20.93, 78.57) * mm});
            skLineSegment(sketch, "E817", {"start": v(20.93, 78.57) * mm, "end": v(21.01, 78.6) * mm});
            skLineSegment(sketch, "E818", {"start": v(21.01, 78.6) * mm, "end": v(21.25, 78.73) * mm});
            skLineSegment(sketch, "E819", {"start": v(21.25, 78.73) * mm, "end": v(21.94, 79.12) * mm});
            skLineSegment(sketch, "E820", {"start": v(21.94, 79.12) * mm, "end": v(22.72, 79.6) * mm});
            skLineSegment(sketch, "E821", {"start": v(22.72, 79.6) * mm, "end": v(23.33, 80) * mm});
            skLineSegment(sketch, "E822", {"start": v(23.33, 80) * mm, "end": v(23.66, 80.24) * mm});
            skLineSegment(sketch, "E823", {"start": v(23.66, 80.24) * mm, "end": v(23.77, 80.32) * mm});
            skLineSegment(sketch, "E824", {"start": v(23.77, 80.32) * mm, "end": v(23.75, 80.2) * mm});
            skLineSegment(sketch, "E825", {"start": v(23.75, 80.2) * mm, "end": v(23.7, 79.85) * mm});
            skLineSegment(sketch, "E826", {"start": v(23.7, 79.85) * mm, "end": v(23.6, 79.35) * mm});
            skLineSegment(sketch, "E827", {"start": v(23.6, 79.35) * mm, "end": v(23.43, 78.75) * mm});
            skLineSegment(sketch, "E828", {"start": v(23.43, 78.75) * mm, "end": v(23.16, 78.11) * mm});
            skLineSegment(sketch, "E829", {"start": v(23.16, 78.11) * mm, "end": v(22.78, 77.49) * mm});
            skLineSegment(sketch, "E830", {"start": v(22.78, 77.49) * mm, "end": v(22.26, 76.93) * mm});
            skLineSegment(sketch, "E831", {"start": v(22.26, 76.93) * mm, "end": v(21.77, 76.59) * mm});
            skLineSegment(sketch, "E832", {"start": v(21.77, 76.59) * mm, "end": v(21.6, 76.5) * mm});
            skLineSegment(sketch, "E833", {"start": v(21.6, 76.5) * mm, "end": v(21.29, 76.36) * mm});
            skLineSegment(sketch, "E834", {"start": v(21.29, 76.36) * mm, "end": v(20.35, 75.97) * mm});
            skLineSegment(sketch, "E835", {"start": v(20.35, 75.97) * mm, "end": v(19.25, 75.6) * mm});
            skLineSegment(sketch, "E836", {"start": v(19.25, 75.6) * mm, "end": v(18.22, 75.32) * mm});
            skLineSegment(sketch, "E837", {"start": v(18.22, 75.32) * mm, "end": v(17.44, 75.15) * mm});
            skLineSegment(sketch, "E838", {"start": v(17.44, 75.15) * mm, "end": v(17.18, 75.1) * mm});
            skLineSegment(sketch, "E839", {"start": v(17.18, 75.1) * mm, "end": v(17.13, 75.09) * mm});
            skLineSegment(sketch, "E840", {"start": v(17.13, 75.09) * mm, "end": v(16.6, 74.96) * mm});
            skLineSegment(sketch, "E841", {"start": v(16.6, 74.96) * mm, "end": v(16.56, 74.95) * mm});
            skLineSegment(sketch, "E842", {"start": v(16.56, 74.95) * mm, "end": v(16.14, 74.88) * mm});
            skLineSegment(sketch, "E843", {"start": v(16.14, 74.88) * mm, "end": v(14.9, 74.64) * mm});
            skLineSegment(sketch, "E844", {"start": v(14.9, 74.64) * mm, "end": v(13.52, 74.37) * mm});
            skLineSegment(sketch, "E845", {"start": v(13.52, 74.37) * mm, "end": v(12.4, 74.14) * mm});
            skLineSegment(sketch, "E846", {"start": v(12.4, 74.14) * mm, "end": v(11.48, 73.93) * mm});
            skLineSegment(sketch, "E847", {"start": v(11.48, 73.93) * mm, "end": v(10.75, 73.72) * mm});
            skLineSegment(sketch, "E848", {"start": v(10.75, 73.72) * mm, "end": v(10.18, 73.52) * mm});
            skLineSegment(sketch, "E849", {"start": v(10.18, 73.52) * mm, "end": v(9.72, 73.32) * mm});
            skLineSegment(sketch, "E850", {"start": v(9.72, 73.32) * mm, "end": v(9.44, 73.15) * mm});
            skLineSegment(sketch, "E851", {"start": v(9.44, 73.15) * mm, "end": v(9.36, 73.09) * mm});
            skLineSegment(sketch, "E852", {"start": v(9.36, 73.09) * mm, "end": v(9.34, 73.07) * mm});
            skLineSegment(sketch, "E853", {"start": v(9.34, 73.07) * mm, "end": v(9.16, 72.93) * mm});
            skLineSegment(sketch, "E854", {"start": v(9.16, 72.93) * mm, "end": v(8.98, 72.8) * mm});
            skLineSegment(sketch, "E855", {"start": v(8.98, 72.8) * mm, "end": v(8.96, 72.78) * mm});
            skLineSegment(sketch, "E856", {"start": v(8.96, 72.78) * mm, "end": v(8.85, 72.67) * mm});
            skLineSegment(sketch, "E857", {"start": v(8.85, 72.67) * mm, "end": v(8.53, 72.32) * mm});
            skLineSegment(sketch, "E858", {"start": v(8.53, 72.32) * mm, "end": v(8.1, 71.8) * mm});
            skLineSegment(sketch, "E859", {"start": v(8.1, 71.8) * mm, "end": v(7.67, 71.17) * mm});
            skLineSegment(sketch, "E860", {"start": v(7.67, 71.17) * mm, "end": v(7.18, 70.43) * mm});
            skLineSegment(sketch, "E861", {"start": v(7.18, 70.43) * mm, "end": v(6.6, 69.55) * mm});
            skLineSegment(sketch, "E862", {"start": v(6.6, 69.55) * mm, "end": v(5.92, 68.5) * mm});
            skLineSegment(sketch, "E863", {"start": v(5.92, 68.5) * mm, "end": v(5.09, 67.26) * mm});
            skLineSegment(sketch, "E864", {"start": v(5.09, 67.26) * mm, "end": v(4.33, 66.17) * mm});
            skLineSegment(sketch, "E865", {"start": v(4.33, 66.17) * mm, "end": v(4.08, 65.8) * mm});
            skLineSegment(sketch, "E866", {"start": v(4.08, 65.8) * mm, "end": v(3.74, 65.32) * mm});
            skLineSegment(sketch, "E867", {"start": v(3.74, 65.32) * mm, "end": v(2.65, 63.94) * mm});
            skLineSegment(sketch, "E868", {"start": v(2.65, 63.94) * mm, "end": v(1.36, 62.55) * mm});
            skLineSegment(sketch, "E869", {"start": v(1.36, 62.55) * mm, "end": v(0.23, 61.57) * mm});
            skLineSegment(sketch, "E870", {"start": v(0.23, 61.57) * mm, "end": v(-0.76, 60.93) * mm});
            skLineSegment(sketch, "E871", {"start": v(-0.76, 60.93) * mm, "end": v(-1.6, 60.56) * mm});
            skLineSegment(sketch, "E872", {"start": v(-1.6, 60.56) * mm, "end": v(-2.3, 60.38) * mm});
            skLineSegment(sketch, "E873", {"start": v(-2.3, 60.38) * mm, "end": v(-2.85, 60.33) * mm});
            skLineSegment(sketch, "E874", {"start": v(-2.85, 60.33) * mm, "end": v(-3.16, 60.33) * mm});
            skLineSegment(sketch, "E875", {"start": v(-3.16, 60.33) * mm, "end": v(-3.26, 60.33) * mm});
            skLineSegment(sketch, "E876", {"start": v(-3.26, 60.33) * mm, "end": v(-3.13, 60.4) * mm});
            skLineSegment(sketch, "E877", {"start": v(-3.13, 60.4) * mm, "end": v(-2.77, 60.64) * mm});
            skLineSegment(sketch, "E878", {"start": v(-2.77, 60.64) * mm, "end": v(-2.22, 61.02) * mm});
            skLineSegment(sketch, "E879", {"start": v(-2.22, 61.02) * mm, "end": v(-1.53, 61.54) * mm});
            skLineSegment(sketch, "E880", {"start": v(-1.53, 61.54) * mm, "end": v(-0.75, 62.2) * mm});
            skLineSegment(sketch, "E881", {"start": v(-0.75, 62.2) * mm, "end": v(0.09, 63) * mm});
            skLineSegment(sketch, "E882", {"start": v(0.09, 63) * mm, "end": v(0.93, 63.91) * mm});
            skLineSegment(sketch, "E883", {"start": v(0.93, 63.91) * mm, "end": v(1.54, 64.68) * mm});
            skLineSegment(sketch, "E884", {"start": v(1.54, 64.68) * mm, "end": v(1.73, 64.95) * mm});
            skLineSegment(sketch, "E885", {"start": v(25.64, 77.54) * mm, "end": v(25.6, 77.5) * mm});
            skLineSegment(sketch, "E886", {"start": v(25.6, 77.5) * mm, "end": v(25.31, 77.35) * mm});
            skLineSegment(sketch, "E887", {"start": v(25.31, 77.35) * mm, "end": v(24.96, 77.18) * mm});
            skLineSegment(sketch, "E888", {"start": v(24.96, 77.18) * mm, "end": v(24.88, 77.14) * mm});
            skLineSegment(sketch, "E889", {"start": v(24.88, 77.14) * mm, "end": v(25, 77.4) * mm});
            skLineSegment(sketch, "E890", {"start": v(25, 77.4) * mm, "end": v(25.32, 78.17) * mm});
            skLineSegment(sketch, "E891", {"start": v(25.32, 78.17) * mm, "end": v(25.57, 79.1) * mm});
            skLineSegment(sketch, "E892", {"start": v(25.57, 79.1) * mm, "end": v(25.7, 79.82) * mm});
            skLineSegment(sketch, "E893", {"start": v(25.7, 79.82) * mm, "end": v(25.73, 80.14) * mm});
            skLineSegment(sketch, "E894", {"start": v(25.73, 80.14) * mm, "end": v(25.73, 80.2) * mm});
            skLineSegment(sketch, "E895", {"start": v(25.73, 80.2) * mm, "end": v(26, 84.73) * mm});
            skLineSegment(sketch, "E896", {"start": v(26, 84.73) * mm, "end": v(22.51, 81.84) * mm});
            skLineSegment(sketch, "E897", {"start": v(22.51, 81.84) * mm, "end": v(22.45, 81.79) * mm});
            skLineSegment(sketch, "E898", {"start": v(22.45, 81.79) * mm, "end": v(22.23, 81.63) * mm});
            skLineSegment(sketch, "E899", {"start": v(22.23, 81.63) * mm, "end": v(21.74, 81.3) * mm});
            skLineSegment(sketch, "E900", {"start": v(21.74, 81.3) * mm, "end": v(21.05, 80.88) * mm});
            skLineSegment(sketch, "E901", {"start": v(21.05, 80.88) * mm, "end": v(20.36, 80.5) * mm});
            skLineSegment(sketch, "E902", {"start": v(20.36, 80.5) * mm, "end": v(20.13, 80.37) * mm});
            skLineSegment(sketch, "E903", {"start": v(20.13, 80.37) * mm, "end": v(20.03, 80.32) * mm});
            skLineSegment(sketch, "E904", {"start": v(20.03, 80.32) * mm, "end": v(19.5, 80.1) * mm});
            skLineSegment(sketch, "E905", {"start": v(19.5, 80.1) * mm, "end": v(18.23, 79.6) * mm});
            skLineSegment(sketch, "E906", {"start": v(18.23, 79.6) * mm, "end": v(16.3, 78.96) * mm});
            skLineSegment(sketch, "E907", {"start": v(16.3, 78.96) * mm, "end": v(14.36, 78.39) * mm});
            skLineSegment(sketch, "E908", {"start": v(14.36, 78.39) * mm, "end": v(13.7, 78.22) * mm});
            skLineSegment(sketch, "E909", {"start": v(13.7, 78.22) * mm, "end": v(13.18, 78.08) * mm});
            skLineSegment(sketch, "E910", {"start": v(13.18, 78.08) * mm, "end": v(11.62, 77.64) * mm});
            skLineSegment(sketch, "E911", {"start": v(11.62, 77.64) * mm, "end": v(9.83, 77.04) * mm});
            skLineSegment(sketch, "E912", {"start": v(9.83, 77.04) * mm, "end": v(8.31, 76.36) * mm});
            skLineSegment(sketch, "E913", {"start": v(8.31, 76.36) * mm, "end": v(7.35, 75.8) * mm});
            skLineSegment(sketch, "E914", {"start": v(7.35, 75.8) * mm, "end": v(7.06, 75.57) * mm});
            skLineSegment(sketch, "E915", {"start": v(7.06, 75.57) * mm, "end": v(7.05, 75.56) * mm});
            skLineSegment(sketch, "E916", {"start": v(7.05, 75.56) * mm, "end": v(6.93, 75.47) * mm});
            skLineSegment(sketch, "E917", {"start": v(6.93, 75.47) * mm, "end": v(6.92, 75.46) * mm});
            skLineSegment(sketch, "E918", {"start": v(6.92, 75.46) * mm, "end": v(6.92, 75.46) * mm});
            skLineSegment(sketch, "E919", {"start": v(6.92, 75.46) * mm, "end": v(6.86, 75.42) * mm});
            skLineSegment(sketch, "E920", {"start": v(6.86, 75.42) * mm, "end": v(6.82, 75.38) * mm});
            skLineSegment(sketch, "E921", {"start": v(6.82, 75.38) * mm, "end": v(6.78, 75.35) * mm});
            skLineSegment(sketch, "E922", {"start": v(6.78, 75.35) * mm, "end": v(6.36, 74.98) * mm});
            skLineSegment(sketch, "E923", {"start": v(6.36, 74.98) * mm, "end": v(6.32, 74.94) * mm});
            skLineSegment(sketch, "E924", {"start": v(6.32, 74.94) * mm, "end": v(6.32, 74.94) * mm});
            skLineSegment(sketch, "E925", {"start": v(6.32, 74.94) * mm, "end": v(6.28, 74.9) * mm});
            skLineSegment(sketch, "E926", {"start": v(6.28, 74.9) * mm, "end": v(6.27, 74.9) * mm});
            skLineSegment(sketch, "E927", {"start": v(6.27, 74.9) * mm, "end": v(6.26, 74.88) * mm});
            skLineSegment(sketch, "E928", {"start": v(6.26, 74.88) * mm, "end": v(6.07, 74.68) * mm});
            skLineSegment(sketch, "E929", {"start": v(6.07, 74.68) * mm, "end": v(6.05, 74.66) * mm});
            skLineSegment(sketch, "E930", {"start": v(6.05, 74.66) * mm, "end": v(6.04, 74.65) * mm});
            skLineSegment(sketch, "E931", {"start": v(6.04, 74.65) * mm, "end": v(5.96, 74.57) * mm});
            skLineSegment(sketch, "E932", {"start": v(5.96, 74.57) * mm, "end": v(5.95, 74.56) * mm});
            skLineSegment(sketch, "E933", {"start": v(5.95, 74.56) * mm, "end": v(5.95, 74.55) * mm});
            skLineSegment(sketch, "E934", {"start": v(5.95, 74.55) * mm, "end": v(5.9, 74.5) * mm});
            skLineSegment(sketch, "E935", {"start": v(5.9, 74.5) * mm, "end": v(5.9, 74.5) * mm});
            skLineSegment(sketch, "E936", {"start": v(5.9, 74.5) * mm, "end": v(5.84, 74.43) * mm});
            skLineSegment(sketch, "E937", {"start": v(5.84, 74.43) * mm, "end": v(5.33, 73.75) * mm});
            skLineSegment(sketch, "E938", {"start": v(5.33, 73.75) * mm, "end": v(5.28, 73.68) * mm});
            skLineSegment(sketch, "E939", {"start": v(5.28, 73.68) * mm, "end": v(5.27, 73.65) * mm});
            skLineSegment(sketch, "E940", {"start": v(5.27, 73.65) * mm, "end": v(5.12, 73.4) * mm});
            skLineSegment(sketch, "E941", {"start": v(5.12, 73.4) * mm, "end": v(5.11, 73.38) * mm});
            skLineSegment(sketch, "E942", {"start": v(5.11, 73.38) * mm, "end": v(5.02, 73.25) * mm});
            skLineSegment(sketch, "E943", {"start": v(5.02, 73.25) * mm, "end": v(4.75, 72.83) * mm});
            skLineSegment(sketch, "E944", {"start": v(4.75, 72.83) * mm, "end": v(4.27, 72.12) * mm});
            skLineSegment(sketch, "E945", {"start": v(4.27, 72.12) * mm, "end": v(3.7, 71.27) * mm});
            skLineSegment(sketch, "E946", {"start": v(3.7, 71.27) * mm, "end": v(3.05, 70.32) * mm});
            skLineSegment(sketch, "E947", {"start": v(3.05, 70.32) * mm, "end": v(2.35, 69.3) * mm});
            skLineSegment(sketch, "E948", {"start": v(2.35, 69.3) * mm, "end": v(1.61, 68.23) * mm});
            skLineSegment(sketch, "E949", {"start": v(1.61, 68.23) * mm, "end": v(0.86, 67.14) * mm});
            skLineSegment(sketch, "E950", {"start": v(0.86, 67.14) * mm, "end": v(0.3, 66.34) * mm});
            skLineSegment(sketch, "E951", {"start": v(0.3, 66.34) * mm, "end": v(0.12, 66.08) * mm});
            skLineSegment(sketch, "E952", {"start": v(0.12, 66.08) * mm, "end": v(-0.04, 65.85) * mm});
            skLineSegment(sketch, "E953", {"start": v(-0.04, 65.85) * mm, "end": v(-0.57, 65.18) * mm});
            skLineSegment(sketch, "E954", {"start": v(-0.57, 65.18) * mm, "end": v(-1.3, 64.39) * mm});
            skLineSegment(sketch, "E955", {"start": v(-1.3, 64.39) * mm, "end": v(-2.03, 63.7) * mm});
            skLineSegment(sketch, "E956", {"start": v(-2.03, 63.7) * mm, "end": v(-2.71, 63.12) * mm});
            skLineSegment(sketch, "E957", {"start": v(-2.71, 63.12) * mm, "end": v(-3.32, 62.66) * mm});
            skLineSegment(sketch, "E958", {"start": v(-3.32, 62.66) * mm, "end": v(-3.8, 62.32) * mm});
            skLineSegment(sketch, "E959", {"start": v(-3.8, 62.32) * mm, "end": v(-4.12, 62.1) * mm});
            skLineSegment(sketch, "E960", {"start": v(-4.12, 62.1) * mm, "end": v(-4.24, 62.04) * mm});
            skLineSegment(sketch, "E961", {"start": v(-4.24, 62.04) * mm, "end": v(-4.24, 62.03) * mm});
            skLineSegment(sketch, "E962", {"start": v(-4.24, 62.03) * mm, "end": v(-4.42, 61.93) * mm});
            skLineSegment(sketch, "E963", {"start": v(-4.42, 61.93) * mm, "end": v(-4.5, 62) * mm});
            skLineSegment(sketch, "E964", {"start": v(-4.5, 62) * mm, "end": v(-4.72, 62.22) * mm});
            skLineSegment(sketch, "E965", {"start": v(-4.72, 62.22) * mm, "end": v(-5.1, 62.66) * mm});
            skLineSegment(sketch, "E966", {"start": v(-5.1, 62.66) * mm, "end": v(-5.63, 63.35) * mm});
            skLineSegment(sketch, "E967", {"start": v(-5.63, 63.35) * mm, "end": v(-6.23, 64.15) * mm});
            skLineSegment(sketch, "E968", {"start": v(-6.23, 64.15) * mm, "end": v(-6.43, 64.41) * mm});
            skLineSegment(sketch, "E969", {"start": v(-6.43, 64.41) * mm, "end": v(-7.02, 65.19) * mm});
            skLineSegment(sketch, "E970", {"start": v(-7.02, 65.19) * mm, "end": v(-7.14, 65.35) * mm});
            skLineSegment(sketch, "E971", {"start": v(-7.14, 65.35) * mm, "end": v(-7.7, 66.14) * mm});
            skLineSegment(sketch, "E972", {"start": v(-7.7, 66.14) * mm, "end": v(-8.26, 66.97) * mm});
            skLineSegment(sketch, "E973", {"start": v(-8.26, 66.97) * mm, "end": v(-8.38, 67.15) * mm});
            skLineSegment(sketch, "E974", {"start": v(-8.38, 67.15) * mm, "end": v(-8.43, 67.23) * mm});
            skLineSegment(sketch, "E975", {"start": v(-8.43, 67.23) * mm, "end": v(-8.95, 68) * mm});
            skLineSegment(sketch, "E976", {"start": v(-8.95, 68) * mm, "end": v(-9, 68.08) * mm});
            skLineSegment(sketch, "E977", {"start": v(-9, 68.08) * mm, "end": v(-9.12, 68.26) * mm});
            skLineSegment(sketch, "E978", {"start": v(-9.12, 68.26) * mm, "end": v(-10.28, 70.21) * mm});
            skLineSegment(sketch, "E979", {"start": v(-10.28, 70.21) * mm, "end": v(-10.4, 70.42) * mm});
            skLineSegment(sketch, "E980", {"start": v(-10.4, 70.42) * mm, "end": v(-10.66, 70.88) * mm});
            skLineSegment(sketch, "E981", {"start": v(-10.66, 70.88) * mm, "end": v(-11.45, 72.24) * mm});
            skLineSegment(sketch, "E982", {"start": v(-11.45, 72.24) * mm, "end": v(-12.66, 74) * mm});
            skLineSegment(sketch, "E983", {"start": v(-12.66, 74) * mm, "end": v(-14.1, 75.56) * mm});
            skLineSegment(sketch, "E984", {"start": v(-14.1, 75.56) * mm, "end": v(-15.4, 76.51) * mm});
            skLineSegment(sketch, "E985", {"start": v(-15.4, 76.51) * mm, "end": v(-15.88, 76.74) * mm});
            skLineSegment(sketch, "E986", {"start": v(-15.88, 76.74) * mm, "end": v(-15.93, 76.77) * mm});
            skLineSegment(sketch, "E987", {"start": v(-15.93, 76.77) * mm, "end": v(-16.5, 77.03) * mm});
            skLineSegment(sketch, "E988", {"start": v(-16.5, 77.03) * mm, "end": v(-16.55, 77.06) * mm});
            skLineSegment(sketch, "E989", {"start": v(-16.55, 77.06) * mm, "end": v(-16.85, 77.2) * mm});
            skLineSegment(sketch, "E990", {"start": v(-16.85, 77.2) * mm, "end": v(-17.75, 77.63) * mm});
            skLineSegment(sketch, "E991", {"start": v(-17.75, 77.63) * mm, "end": v(-19.22, 78.3) * mm});
            skLineSegment(sketch, "E992", {"start": v(-19.22, 78.3) * mm, "end": v(-21.08, 79.06) * mm});
            skLineSegment(sketch, "E993", {"start": v(-21.08, 79.06) * mm, "end": v(-22.87, 79.74) * mm});
            skLineSegment(sketch, "E994", {"start": v(-22.87, 79.74) * mm, "end": v(-23.47, 79.95) * mm});
            skLineSegment(sketch, "E995", {"start": v(-23.47, 79.95) * mm, "end": v(-23.95, 80.13) * mm});
            skLineSegment(sketch, "E996", {"start": v(-23.95, 80.13) * mm, "end": v(-25.4, 80.67) * mm});
            skLineSegment(sketch, "E997", {"start": v(-25.4, 80.67) * mm, "end": v(-27.12, 81.36) * mm});
            skLineSegment(sketch, "E998", {"start": v(-27.12, 81.36) * mm, "end": v(-28.6, 82) * mm});
            skLineSegment(sketch, "E999", {"start": v(-28.6, 82) * mm, "end": v(-29.87, 82.56) * mm});
            skLineSegment(sketch, "E1000", {"start": v(-29.87, 82.56) * mm, "end": v(-30.9, 83.05) * mm});
            skLineSegment(sketch, "E1001", {"start": v(-30.9, 83.05) * mm, "end": v(-31.68, 83.45) * mm});
            skLineSegment(sketch, "E1002", {"start": v(-31.68, 83.45) * mm, "end": v(-32.23, 83.74) * mm});
            skLineSegment(sketch, "E1003", {"start": v(-32.23, 83.74) * mm, "end": v(-32.46, 83.87) * mm});
            skLineSegment(sketch, "E1004", {"start": v(-32.46, 83.87) * mm, "end": v(-32.54, 83.91) * mm});
            skLineSegment(sketch, "E1005", {"start": v(-32.54, 83.91) * mm, "end": v(-32.87, 84.13) * mm});
            skLineSegment(sketch, "E1006", {"start": v(-32.87, 84.13) * mm, "end": v(-33.84, 84.78) * mm});
            skLineSegment(sketch, "E1007", {"start": v(-33.84, 84.78) * mm, "end": v(-34.88, 85.52) * mm});
            skLineSegment(sketch, "E1008", {"start": v(-34.88, 85.52) * mm, "end": v(-35.65, 86.11) * mm});
            skLineSegment(sketch, "E1009", {"start": v(-35.65, 86.11) * mm, "end": v(-36.02, 86.42) * mm});
            skLineSegment(sketch, "E1010", {"start": v(-36.02, 86.42) * mm, "end": v(-36.14, 86.53) * mm});
            skLineSegment(sketch, "E1011", {"start": v(-36.14, 86.53) * mm, "end": v(-39.81, 89.97) * mm});
            skLineSegment(sketch, "E1012", {"start": v(-39.81, 89.97) * mm, "end": v(-39.45, 84.95) * mm});
            skLineSegment(sketch, "E1013", {"start": v(-39.45, 84.95) * mm, "end": v(-39.44, 84.85) * mm});
            skLineSegment(sketch, "E1014", {"start": v(-39.44, 84.85) * mm, "end": v(-39.4, 84.53) * mm});
            skLineSegment(sketch, "E1015", {"start": v(-39.4, 84.53) * mm, "end": v(-39.3, 83.77) * mm});
            skLineSegment(sketch, "E1016", {"start": v(-39.3, 83.77) * mm, "end": v(-39.07, 82.76) * mm});
            skLineSegment(sketch, "E1017", {"start": v(-39.07, 82.76) * mm, "end": v(-38.71, 81.6) * mm});
            skLineSegment(sketch, "E1018", {"start": v(-38.71, 81.6) * mm, "end": v(-38.18, 80.36) * mm});
            skLineSegment(sketch, "E1019", {"start": v(-38.18, 80.36) * mm, "end": v(-37.44, 79.15) * mm});
            skLineSegment(sketch, "E1020", {"start": v(-37.44, 79.15) * mm, "end": v(-36.47, 78.06) * mm});
            skLineSegment(sketch, "E1021", {"start": v(-36.47, 78.06) * mm, "end": v(-35.56, 77.37) * mm});
            skLineSegment(sketch, "E1022", {"start": v(-35.56, 77.37) * mm, "end": v(-35.23, 77.19) * mm});
            skLineSegment(sketch, "E1023", {"start": v(-35.23, 77.19) * mm, "end": v(-35.16, 77.15) * mm});
            skLineSegment(sketch, "E1024", {"start": v(-35.16, 77.15) * mm, "end": v(-34.47, 76.78) * mm});
            skLineSegment(sketch, "E1025", {"start": v(-34.47, 76.78) * mm, "end": v(-34.4, 76.74) * mm});
            skLineSegment(sketch, "E1026", {"start": v(-34.4, 76.74) * mm, "end": v(-34.81, 76.87) * mm});
            skLineSegment(sketch, "E1027", {"start": v(-34.81, 76.87) * mm, "end": v(-36.02, 77.29) * mm});
            skLineSegment(sketch, "E1028", {"start": v(-36.02, 77.29) * mm, "end": v(-37.56, 77.85) * mm});
            skLineSegment(sketch, "E1029", {"start": v(-37.56, 77.85) * mm, "end": v(-39, 78.4) * mm});
            skLineSegment(sketch, "E1030", {"start": v(-39, 78.4) * mm, "end": v(-40.32, 78.96) * mm});
            skLineSegment(sketch, "E1031", {"start": v(-40.32, 78.96) * mm, "end": v(-41.52, 79.5) * mm});
            skLineSegment(sketch, "E1032", {"start": v(-41.52, 79.5) * mm, "end": v(-42.55, 80) * mm});
            skLineSegment(sketch, "E1033", {"start": v(-42.55, 80) * mm, "end": v(-43.41, 80.44) * mm});
            skLineSegment(sketch, "E1034", {"start": v(-43.41, 80.44) * mm, "end": v(-43.91, 80.73) * mm});
            skLineSegment(sketch, "E1035", {"start": v(-43.91, 80.73) * mm, "end": v(-44.07, 80.83) * mm});
            skLineSegment(sketch, "E1036", {"start": v(-44.07, 80.83) * mm, "end": v(-48.12, 83.4) * mm});
            skLineSegment(sketch, "E1037", {"start": v(-48.12, 83.4) * mm, "end": v(-47.05, 78.73) * mm});
            skLineSegment(sketch, "E1038", {"start": v(-47.05, 78.73) * mm, "end": v(-47.02, 78.6) * mm});
            skLineSegment(sketch, "E1039", {"start": v(-47.02, 78.6) * mm, "end": v(-46.93, 78.25) * mm});
            skLineSegment(sketch, "E1040", {"start": v(-46.93, 78.25) * mm, "end": v(-46.7, 77.51) * mm});
            skLineSegment(sketch, "E1041", {"start": v(-46.7, 77.51) * mm, "end": v(-46.38, 76.6) * mm});
            skLineSegment(sketch, "E1042", {"start": v(-46.38, 76.6) * mm, "end": v(-45.94, 75.58) * mm});
            skLineSegment(sketch, "E1043", {"start": v(-45.94, 75.58) * mm, "end": v(-45.37, 74.55) * mm});
            skLineSegment(sketch, "E1044", {"start": v(-45.37, 74.55) * mm, "end": v(-44.66, 73.57) * mm});
            skLineSegment(sketch, "E1045", {"start": v(-44.66, 73.57) * mm, "end": v(-43.8, 72.73) * mm});
            skLineSegment(sketch, "E1046", {"start": v(-43.8, 72.73) * mm, "end": v(-43.06, 72.22) * mm});
            skLineSegment(sketch, "E1047", {"start": v(-43.06, 72.22) * mm, "end": v(-42.8, 72.1) * mm});
            skLineSegment(sketch, "E1048", {"start": v(-42.8, 72.1) * mm, "end": v(-42.65, 72.03) * mm});
            skLineSegment(sketch, "E1049", {"start": v(-42.65, 72.03) * mm, "end": v(-41.2, 71.41) * mm});
            skLineSegment(sketch, "E1050", {"start": v(-41.2, 71.41) * mm, "end": v(-41.05, 71.36) * mm});
            skLineSegment(sketch, "E1051", {"start": v(-41.05, 71.36) * mm, "end": v(-41.54, 71.45) * mm});
            skLineSegment(sketch, "E1052", {"start": v(-41.54, 71.45) * mm, "end": v(-43, 71.77) * mm});
            skLineSegment(sketch, "E1053", {"start": v(-43, 71.77) * mm, "end": v(-44.66, 72.18) * mm});
            skLineSegment(sketch, "E1054", {"start": v(-44.66, 72.18) * mm, "end": v(-45.95, 72.54) * mm});
            skLineSegment(sketch, "E1055", {"start": v(-45.95, 72.54) * mm, "end": v(-46.6, 72.75) * mm});
            skLineSegment(sketch, "E1056", {"start": v(-46.6, 72.75) * mm, "end": v(-46.8, 72.83) * mm});
            skLineSegment(sketch, "E1057", {"start": v(-46.8, 72.83) * mm, "end": v(-50.7, 74.31) * mm});
            skLineSegment(sketch, "E1058", {"start": v(-50.7, 74.31) * mm, "end": v(-49.37, 70.36) * mm});
            skLineSegment(sketch, "E1059", {"start": v(-49.37, 70.36) * mm, "end": v(-49.35, 70.28) * mm});
            skLineSegment(sketch, "E1060", {"start": v(-49.35, 70.28) * mm, "end": v(-49.25, 70.02) * mm});
            skLineSegment(sketch, "E1061", {"start": v(-49.25, 70.02) * mm, "end": v(-49.05, 69.52) * mm});
            skLineSegment(sketch, "E1062", {"start": v(-49.05, 69.52) * mm, "end": v(-48.78, 68.9) * mm});
            skLineSegment(sketch, "E1063", {"start": v(-48.78, 68.9) * mm, "end": v(-48.43, 68.2) * mm});
            skLineSegment(sketch, "E1064", {"start": v(-48.43, 68.2) * mm, "end": v(-48, 67.45) * mm});
            skLineSegment(sketch, "E1065", {"start": v(-48, 67.45) * mm, "end": v(-47.5, 66.7) * mm});
            skLineSegment(sketch, "E1066", {"start": v(-47.5, 66.7) * mm, "end": v(-46.9, 65.98) * mm});
            skLineSegment(sketch, "E1067", {"start": v(-46.9, 65.98) * mm, "end": v(-46.41, 65.49) * mm});
            skLineSegment(sketch, "E1068", {"start": v(-46.41, 65.49) * mm, "end": v(-46.23, 65.34) * mm});
            skLineSegment(sketch, "E1069", {"start": v(-46.23, 65.34) * mm, "end": v(-46.7, 65.45) * mm});
            skLineSegment(sketch, "E1070", {"start": v(-46.7, 65.45) * mm, "end": v(-43.84, 61.25) * mm});
            skLineSegment(sketch, "E1071", {"start": v(-43.84, 61.25) * mm, "end": v(-43.79, 61.17) * mm});
            skLineSegment(sketch, "E1072", {"start": v(-43.79, 61.17) * mm, "end": v(-43.62, 60.94) * mm});
            skLineSegment(sketch, "E1073", {"start": v(-43.62, 60.94) * mm, "end": v(-43.25, 60.47) * mm});
            skLineSegment(sketch, "E1074", {"start": v(-43.25, 60.47) * mm, "end": v(-42.75, 59.9) * mm});
            skLineSegment(sketch, "E1075", {"start": v(-42.75, 59.9) * mm, "end": v(-42.13, 59.29) * mm});
            skLineSegment(sketch, "E1076", {"start": v(-42.13, 59.29) * mm, "end": v(-41.4, 58.7) * mm});
            skLineSegment(sketch, "E1077", {"start": v(-41.4, 58.7) * mm, "end": v(-40.6, 58.17) * mm});
            skLineSegment(sketch, "E1078", {"start": v(-40.6, 58.17) * mm, "end": v(-39.7, 57.78) * mm});
            skLineSegment(sketch, "E1079", {"start": v(-39.7, 57.78) * mm, "end": v(-39, 57.6) * mm});
            skLineSegment(sketch, "E1080", {"start": v(-39, 57.6) * mm, "end": v(-38.75, 57.57) * mm});
            skLineSegment(sketch, "E1081", {"start": v(-38.75, 57.57) * mm, "end": v(-38.66, 57.57) * mm});
            skLineSegment(sketch, "E1082", {"start": v(-38.66, 57.57) * mm, "end": v(-37.87, 57.52) * mm});
            skLineSegment(sketch, "E1083", {"start": v(-37.87, 57.52) * mm, "end": v(-37.6, 57.52) * mm});
            skLineSegment(sketch, "E1084", {"start": v(-37.6, 57.52) * mm, "end": v(-37.4, 57.52) * mm});
            skLineSegment(sketch, "E1085", {"start": v(-37.4, 57.52) * mm, "end": v(-36.8, 57.47) * mm});
            skLineSegment(sketch, "E1086", {"start": v(-36.8, 57.47) * mm, "end": v(-35.88, 57.35) * mm});
            skLineSegment(sketch, "E1087", {"start": v(-35.88, 57.35) * mm, "end": v(-34.9, 57.17) * mm});
            skLineSegment(sketch, "E1088", {"start": v(-34.9, 57.17) * mm, "end": v(-33.97, 56.96) * mm});
            skLineSegment(sketch, "E1089", {"start": v(-33.97, 56.96) * mm, "end": v(-33.11, 56.76) * mm});
            skLineSegment(sketch, "E1090", {"start": v(-33.11, 56.76) * mm, "end": v(-32.42, 56.58) * mm});
            skLineSegment(sketch, "E1091", {"start": v(-32.42, 56.58) * mm, "end": v(-31.95, 56.45) * mm});
            skLineSegment(sketch, "E1092", {"start": v(-31.95, 56.45) * mm, "end": v(-31.78, 56.4) * mm});
            skLineSegment(sketch, "E1093", {"start": v(-31.78, 56.4) * mm, "end": v(-31.78, 56.4) * mm});
            skLineSegment(sketch, "E1094", {"start": v(-31.78, 56.4) * mm, "end": v(-31.69, 56.4) * mm});
            skLineSegment(sketch, "E1095", {"start": v(-31.69, 56.4) * mm, "end": v(-31.52, 56.4) * mm});
            skLineSegment(sketch, "E1096", {"start": v(-31.52, 56.4) * mm, "end": v(-31.46, 56.4) * mm});
            skLineSegment(sketch, "E1097", {"start": v(-31.46, 56.4) * mm, "end": v(-31, 56.4) * mm});
            skLineSegment(sketch, "E1098", {"start": v(-31, 56.4) * mm, "end": v(-29.62, 56.32) * mm});
            skLineSegment(sketch, "E1099", {"start": v(-29.62, 56.32) * mm, "end": v(-27.7, 56.05) * mm});
            skLineSegment(sketch, "E1100", {"start": v(-27.7, 56.05) * mm, "end": v(-25.91, 55.55) * mm});
            skLineSegment(sketch, "E1101", {"start": v(-25.91, 55.55) * mm, "end": v(-24.78, 55.04) * mm});
            skLineSegment(sketch, "E1102", {"start": v(-24.78, 55.04) * mm, "end": v(-24.45, 54.8) * mm});
            skLineSegment(sketch, "E1103", {"start": v(-24.45, 54.8) * mm, "end": v(-24.29, 54.69) * mm});
            skLineSegment(sketch, "E1104", {"start": v(-24.29, 54.69) * mm, "end": v(-23.44, 54.02) * mm});
            skLineSegment(sketch, "E1105", {"start": v(-23.44, 54.02) * mm, "end": v(-22.53, 53.26) * mm});
            skLineSegment(sketch, "E1106", {"start": v(-22.53, 53.26) * mm, "end": v(-22.34, 53.1) * mm});
            skLineSegment(sketch, "E1107", {"start": v(-22.34, 53.1) * mm, "end": v(-22.02, 52.82) * mm});
            skLineSegment(sketch, "E1108", {"start": v(-22.02, 52.82) * mm, "end": v(-21.04, 52) * mm});
            skLineSegment(sketch, "E1109", {"start": v(-21.04, 52) * mm, "end": v(-19.64, 50.91) * mm});
            skLineSegment(sketch, "E1110", {"start": v(-19.64, 50.91) * mm, "end": v(-18.13, 49.9) * mm});
            skLineSegment(sketch, "E1111", {"start": v(-18.13, 49.9) * mm, "end": v(-16.94, 49.23) * mm});
            skLineSegment(sketch, "E1112", {"start": v(-16.94, 49.23) * mm, "end": v(-16.52, 49.04) * mm});
            skLineSegment(sketch, "E1113", {"start": v(-16.52, 49.04) * mm, "end": v(-17.12, 48.9) * mm});
            skLineSegment(sketch, "E1114", {"start": v(-17.12, 48.9) * mm, "end": v(-18.91, 48.48) * mm});
            skLineSegment(sketch, "E1115", {"start": v(-18.91, 48.48) * mm, "end": v(-21.26, 47.96) * mm});
            skLineSegment(sketch, "E1116", {"start": v(-21.26, 47.96) * mm, "end": v(-23.42, 47.53) * mm});
            skLineSegment(sketch, "E1117", {"start": v(-23.42, 47.53) * mm, "end": v(-24.77, 47.3) * mm});
            skLineSegment(sketch, "E1118", {"start": v(-24.77, 47.3) * mm, "end": v(-25.22, 47.23) * mm});
            skLineSegment(sketch, "E1119", {"start": v(-25.22, 47.23) * mm, "end": v(-28.19, 46.82) * mm});
            skLineSegment(sketch, "E1120", {"start": v(-28.19, 46.82) * mm, "end": v(-26.64, 44.26) * mm});
            skLineSegment(sketch, "E1121", {"start": v(-26.64, 44.26) * mm, "end": v(-26.6, 44.2) * mm});
            skLineSegment(sketch, "E1122", {"start": v(-26.6, 44.2) * mm, "end": v(-26.32, 43.8) * mm});
            skLineSegment(sketch, "E1123", {"start": v(-26.32, 43.8) * mm, "end": v(-25.6, 43) * mm});
            skLineSegment(sketch, "E1124", {"start": v(-25.6, 43) * mm, "end": v(-24.5, 42.16) * mm});
            skLineSegment(sketch, "E1125", {"start": v(-24.5, 42.16) * mm, "end": v(-23.4, 41.66) * mm});
            skLineSegment(sketch, "E1126", {"start": v(-23.4, 41.66) * mm, "end": v(-23.01, 41.59) * mm});
            skLineSegment(sketch, "E1127", {"start": v(-23.01, 41.59) * mm, "end": v(-20.9, 40.14) * mm});
            skLineSegment(sketch, "E1128", {"start": v(-20.9, 40.14) * mm, "end": v(-20.83, 40.09) * mm});
            skLineSegment(sketch, "E1129", {"start": v(-20.83, 40.09) * mm, "end": v(-20.48, 39.87) * mm});
            skLineSegment(sketch, "E1130", {"start": v(-20.48, 39.87) * mm, "end": v(-19.67, 39.47) * mm});
            skLineSegment(sketch, "E1131", {"start": v(-19.67, 39.47) * mm, "end": v(-18.6, 39.11) * mm});
            skLineSegment(sketch, "E1132", {"start": v(-18.6, 39.11) * mm, "end": v(-17.65, 38.95) * mm});
            skLineSegment(sketch, "E1133", {"start": v(-17.65, 38.95) * mm, "end": v(-17.34, 38.95) * mm});
            skLineSegment(sketch, "E1134", {"start": v(-17.34, 38.95) * mm, "end": v(-17.1, 38.95) * mm});
            skLineSegment(sketch, "E1135", {"start": v(-17.1, 38.95) * mm, "end": v(-16.43, 39.04) * mm});
            skLineSegment(sketch, "E1136", {"start": v(-16.43, 39.04) * mm, "end": v(-16.36, 39.06) * mm});
            skLineSegment(sketch, "E1137", {"start": v(-16.36, 39.06) * mm, "end": v(-14.75, 38.43) * mm});
            skLineSegment(sketch, "E1138", {"start": v(-14.75, 38.43) * mm, "end": v(-14.71, 38.42) * mm});
            skLineSegment(sketch, "E1139", {"start": v(-14.71, 38.42) * mm, "end": v(-14.54, 38.36) * mm});
            skLineSegment(sketch, "E1140", {"start": v(-14.54, 38.36) * mm, "end": v(-14.16, 38.26) * mm});
            skLineSegment(sketch, "E1141", {"start": v(-14.16, 38.26) * mm, "end": v(-13.63, 38.16) * mm});
            skLineSegment(sketch, "E1142", {"start": v(-13.63, 38.16) * mm, "end": v(-13.16, 38.12) * mm});
            skLineSegment(sketch, "E1143", {"start": v(-13.16, 38.12) * mm, "end": v(-13, 38.12) * mm});
            skLineSegment(sketch, "E1144", {"start": v(-13, 38.12) * mm, "end": v(-12.68, 38.12) * mm});
            skLineSegment(sketch, "E1145", {"start": v(-12.68, 38.12) * mm, "end": v(-11.74, 38.3) * mm});
            skLineSegment(sketch, "E1146", {"start": v(-11.74, 38.3) * mm, "end": v(-10.8, 38.7) * mm});
            skLineSegment(sketch, "E1147", {"start": v(-10.8, 38.7) * mm, "end": v(-10.64, 38.83) * mm});
            skLineSegment(sketch, "E1148", {"start": v(-10.64, 38.83) * mm, "end": v(-9.07, 39.02) * mm});
            skLineSegment(sketch, "E1149", {"start": v(-9.07, 39.02) * mm, "end": v(-8.85, 39.05) * mm});
            skLineSegment(sketch, "E1150", {"start": v(-8.85, 39.05) * mm, "end": v(-7.82, 39.46) * mm});
            skLineSegment(sketch, "E1151", {"start": v(-7.82, 39.46) * mm, "end": v(-6.94, 40.13) * mm});
            skLineSegment(sketch, "E1152", {"start": v(-6.94, 40.13) * mm, "end": v(-6.8, 40.28) * mm});
            skLineSegment(sketch, "E1153", {"start": v(-6.8, 40.28) * mm, "end": v(-6.92, 39.59) * mm});
            skLineSegment(sketch, "E1154", {"start": v(-6.92, 39.59) * mm, "end": v(-5.05, 40) * mm});
            skLineSegment(sketch, "E1155", {"start": v(-5.05, 40) * mm, "end": v(-5.05, 39.7) * mm});
            skLineSegment(sketch, "E1156", {"start": v(-5.05, 39.7) * mm, "end": v(-5.06, 38.9) * mm});
            skLineSegment(sketch, "E1157", {"start": v(-5.06, 38.9) * mm, "end": v(-5.07, 37.76) * mm});
            skLineSegment(sketch, "E1158", {"start": v(-5.07, 37.76) * mm, "end": v(-5.07, 36.77) * mm});
            skLineSegment(sketch, "E1159", {"start": v(-5.07, 36.77) * mm, "end": v(-5.07, 36.43) * mm});
            skLineSegment(sketch, "E1160", {"start": v(-5.07, 36.43) * mm, "end": v(-5.07, 36.21) * mm});
            skLineSegment(sketch, "E1161", {"start": v(-5.07, 36.21) * mm, "end": v(-4.96, 35.54) * mm});
            skLineSegment(sketch, "E1162", {"start": v(-4.96, 35.54) * mm, "end": v(-4.65, 34.75) * mm});
            skLineSegment(sketch, "E1163", {"start": v(-4.65, 34.75) * mm, "end": v(-4.16, 34.05) * mm});
            skLineSegment(sketch, "E1164", {"start": v(-4.16, 34.05) * mm, "end": v(-3.52, 33.46) * mm});
            skLineSegment(sketch, "E1165", {"start": v(-3.52, 33.46) * mm, "end": v(-2.77, 32.97) * mm});
            skLineSegment(sketch, "E1166", {"start": v(-2.77, 32.97) * mm, "end": v(-1.93, 32.6) * mm});
            skLineSegment(sketch, "E1167", {"start": v(-1.93, 32.6) * mm, "end": v(-1.03, 32.36) * mm});
            skLineSegment(sketch, "E1168", {"start": v(-1.03, 32.36) * mm, "end": v(-0.1, 32.23) * mm});
            skLineSegment(sketch, "E1169", {"start": v(-0.1, 32.23) * mm, "end": v(0.85, 32.24) * mm});
            skLineSegment(sketch, "E1170", {"start": v(0.85, 32.24) * mm, "end": v(1.76, 32.4) * mm});
            skLineSegment(sketch, "E1171", {"start": v(1.76, 32.4) * mm, "end": v(2.63, 32.68) * mm});
            skLineSegment(sketch, "E1172", {"start": v(2.63, 32.68) * mm, "end": v(3.4, 33.12) * mm});
            skLineSegment(sketch, "E1173", {"start": v(3.4, 33.12) * mm, "end": v(4.08, 33.7) * mm});
            skLineSegment(sketch, "E1174", {"start": v(4.08, 33.7) * mm, "end": v(4.61, 34.46) * mm});
            skLineSegment(sketch, "E1175", {"start": v(4.61, 34.46) * mm, "end": v(4.98, 35.37) * mm});
            skLineSegment(sketch, "E1176", {"start": v(4.98, 35.37) * mm, "end": v(5.13, 36.19) * mm});
            skLineSegment(sketch, "E1177", {"start": v(5.13, 36.19) * mm, "end": v(5.15, 36.46) * mm});
            skLineSegment(sketch, "E1178", {"start": v(5.15, 36.46) * mm, "end": v(5.17, 36.8) * mm});
            skLineSegment(sketch, "E1179", {"start": v(5.17, 36.8) * mm, "end": v(5.2, 37.87) * mm});
            skLineSegment(sketch, "E1180", {"start": v(5.2, 37.87) * mm, "end": v(5.19, 38.8) * mm});
            skLineSegment(sketch, "E1181", {"start": v(5.19, 38.8) * mm, "end": v(5.16, 39.3) * mm});
            skLineSegment(sketch, "E1182", {"start": v(5.16, 39.3) * mm, "end": v(5.14, 39.47) * mm});
            skLineSegment(sketch, "E1183", {"start": v(5.14, 39.47) * mm, "end": v(6.8, 39.21) * mm});
            skLineSegment(sketch, "E1184", {"start": v(6.8, 39.21) * mm, "end": v(6.93, 39.18) * mm});
            skLineSegment(sketch, "E1185", {"start": v(6.93, 39.18) * mm, "end": v(7.34, 39.2) * mm});
            skLineSegment(sketch, "E1186", {"start": v(7.34, 39.2) * mm, "end": v(7.7, 39.4) * mm});
            skLineSegment(sketch, "E1187", {"start": v(7.7, 39.4) * mm, "end": v(7.88, 39.8) * mm});
            skLineSegment(sketch, "E1188", {"start": v(7.88, 39.8) * mm, "end": v(7.93, 40.32) * mm});
            skLineSegment(sketch, "E1189", {"start": v(7.93, 40.32) * mm, "end": v(7.87, 40.93) * mm});
            skLineSegment(sketch, "E1190", {"start": v(7.87, 40.93) * mm, "end": v(7.72, 41.56) * mm});
            skLineSegment(sketch, "E1191", {"start": v(7.72, 41.56) * mm, "end": v(7.5, 42.18) * mm});
            skLineSegment(sketch, "E1192", {"start": v(7.5, 42.18) * mm, "end": v(7.3, 42.6) * mm});
            skLineSegment(sketch, "E1193", {"start": v(7.3, 42.6) * mm, "end": v(7.24, 42.74) * mm});
            skLineSegment(sketch, "E1194", {"start": v(7.24, 42.74) * mm, "end": v(7.58, 42.73) * mm});
            skLineSegment(sketch, "E1195", {"start": v(7.58, 42.73) * mm, "end": v(8.36, 42.73) * mm});
            skLineSegment(sketch, "E1196", {"start": v(8.36, 42.73) * mm, "end": v(9.23, 42.8) * mm});
            skLineSegment(sketch, "E1197", {"start": v(9.23, 42.8) * mm, "end": v(9.72, 42.91) * mm});
            skLineSegment(sketch, "E1198", {"start": v(9.72, 42.91) * mm, "end": v(9.84, 43) * mm});
            skLineSegment(sketch, "E1199", {"start": v(9.84, 43) * mm, "end": v(9.88, 43.04) * mm});
            skLineSegment(sketch, "E1200", {"start": v(9.88, 43.04) * mm, "end": v(9.97, 43.2) * mm});
            skLineSegment(sketch, "E1201", {"start": v(9.97, 43.2) * mm, "end": v(10.02, 43.45) * mm});
            skLineSegment(sketch, "E1202", {"start": v(10.02, 43.45) * mm, "end": v(10.01, 43.74) * mm});
            skLineSegment(sketch, "E1203", {"start": v(10.01, 43.74) * mm, "end": v(9.96, 44.04) * mm});
            skLineSegment(sketch, "E1204", {"start": v(9.96, 44.04) * mm, "end": v(9.89, 44.33) * mm});
            skLineSegment(sketch, "E1205", {"start": v(9.89, 44.33) * mm, "end": v(9.8, 44.57) * mm});
            skLineSegment(sketch, "E1206", {"start": v(9.8, 44.57) * mm, "end": v(9.75, 44.73) * mm});
            skLineSegment(sketch, "E1207", {"start": v(9.75, 44.73) * mm, "end": v(9.72, 44.8) * mm});
            skLineSegment(sketch, "E1208", {"start": v(9.72, 44.8) * mm, "end": v(9.58, 45.02) * mm});
            skLineSegment(sketch, "E1209", {"start": v(9.58, 45.02) * mm, "end": v(9.15, 45.7) * mm});
            skLineSegment(sketch, "E1210", {"start": v(9.15, 45.7) * mm, "end": v(8.5, 46.49) * mm});
            skLineSegment(sketch, "E1211", {"start": v(8.5, 46.49) * mm, "end": v(7.66, 47.03) * mm});
            skLineSegment(sketch, "E1212", {"start": v(7.66, 47.03) * mm, "end": v(6.84, 47.24) * mm});
            skLineSegment(sketch, "E1213", {"start": v(6.84, 47.24) * mm, "end": v(6.56, 47.24) * mm});
            skLineSegment(sketch, "E1214", {"start": v(6.56, 47.24) * mm, "end": v(6.34, 47.24) * mm});
            skLineSegment(sketch, "E1215", {"start": v(6.34, 47.24) * mm, "end": v(5.69, 47.13) * mm});
            skLineSegment(sketch, "E1216", {"start": v(5.69, 47.13) * mm, "end": v(4.92, 46.92) * mm});
            skLineSegment(sketch, "E1217", {"start": v(4.92, 46.92) * mm, "end": v(4.75, 46.87) * mm});
            skLineSegment(sketch, "E1218", {"start": v(4.75, 46.87) * mm, "end": v(4.71, 46.9) * mm});
            skLineSegment(sketch, "E1219", {"start": v(4.71, 46.9) * mm, "end": v(4.51, 47.1) * mm});
            skLineSegment(sketch, "E1220", {"start": v(4.51, 47.1) * mm, "end": v(4.36, 47.37) * mm});
            skLineSegment(sketch, "E1221", {"start": v(4.36, 47.37) * mm, "end": v(4.35, 47.42) * mm});
            skLineSegment(sketch, "E1222", {"start": v(4.35, 47.42) * mm, "end": v(4.34, 47.44) * mm});
            skLineSegment(sketch, "E1223", {"start": v(4.34, 47.44) * mm, "end": v(4.33, 47.54) * mm});
            skLineSegment(sketch, "E1224", {"start": v(4.33, 47.54) * mm, "end": v(4.4, 47.68) * mm});
            skLineSegment(sketch, "E1225", {"start": v(4.4, 47.68) * mm, "end": v(4.43, 47.71) * mm});
            skLineSegment(sketch, "E1226", {"start": v(4.43, 47.71) * mm, "end": v(4.58, 47.87) * mm});
            skLineSegment(sketch, "E1227", {"start": v(4.58, 47.87) * mm, "end": v(5.07, 48.33) * mm});
            skLineSegment(sketch, "E1228", {"start": v(5.07, 48.33) * mm, "end": v(5.53, 48.75) * mm});
            skLineSegment(sketch, "E1229", {"start": v(5.53, 48.75) * mm, "end": v(5.83, 49.02) * mm});
            skLineSegment(sketch, "E1230", {"start": v(5.83, 49.02) * mm, "end": v(5.97, 49.14) * mm});
            skLineSegment(sketch, "E1231", {"start": v(5.97, 49.14) * mm, "end": v(6, 49.17) * mm});
            skLineSegment(sketch, "E1232", {"start": v(6, 49.17) * mm, "end": v(6.02, 49.17) * mm});
            skLineSegment(sketch, "E1233", {"start": v(6.02, 49.17) * mm, "end": v(6.17, 49.28) * mm});
            skLineSegment(sketch, "E1234", {"start": v(6.17, 49.28) * mm, "end": v(6.24, 49.33) * mm});
            skLineSegment(sketch, "E1235", {"start": v(6.24, 49.33) * mm, "end": v(6.55, 49.48) * mm});
            skLineSegment(sketch, "E1236", {"start": v(6.55, 49.48) * mm, "end": v(6.76, 49.52) * mm});
            skLineSegment(sketch, "E1237", {"start": v(6.76, 49.52) * mm, "end": v(6.83, 49.52) * mm});
            skLineSegment(sketch, "E1238", {"start": v(6.83, 49.52) * mm, "end": v(6.93, 49.52) * mm});
            skLineSegment(sketch, "E1239", {"start": v(6.93, 49.52) * mm, "end": v(7.23, 49.45) * mm});
            skLineSegment(sketch, "E1240", {"start": v(7.23, 49.45) * mm, "end": v(7.62, 49.3) * mm});
            skLineSegment(sketch, "E1241", {"start": v(7.62, 49.3) * mm, "end": v(7.7, 49.26) * mm});
            skLineSegment(sketch, "E1242", {"start": v(7.7, 49.26) * mm, "end": v(8.47, 50.25) * mm});
            skLineSegment(sketch, "E1243", {"start": v(8.47, 50.25) * mm, "end": v(9.66, 48.14) * mm});
            skLineSegment(sketch, "E1244", {"start": v(9.66, 48.14) * mm, "end": v(9.93, 48.25) * mm});
            skLineSegment(sketch, "E1245", {"start": v(9.93, 48.25) * mm, "end": v(10.73, 48.64) * mm});
            skLineSegment(sketch, "E1246", {"start": v(10.73, 48.64) * mm, "end": v(11.56, 49.17) * mm});
            skLineSegment(sketch, "E1247", {"start": v(11.56, 49.17) * mm, "end": v(12.18, 49.73) * mm});
            skLineSegment(sketch, "E1248", {"start": v(12.18, 49.73) * mm, "end": v(12.62, 50.3) * mm});
            skLineSegment(sketch, "E1249", {"start": v(12.62, 50.3) * mm, "end": v(12.9, 50.84) * mm});
            skLineSegment(sketch, "E1250", {"start": v(12.9, 50.84) * mm, "end": v(13.06, 51.36) * mm});
            skLineSegment(sketch, "E1251", {"start": v(13.06, 51.36) * mm, "end": v(13.12, 51.84) * mm});
            skLineSegment(sketch, "E1252", {"start": v(13.12, 51.84) * mm, "end": v(13.12, 52.15) * mm});
            skLineSegment(sketch, "E1253", {"start": v(13.12, 52.15) * mm, "end": v(13.11, 52.25) * mm});
            skLineSegment(sketch, "E1254", {"start": v(13.11, 52.25) * mm, "end": v(13.1, 52.46) * mm});
            skLineSegment(sketch, "E1255", {"start": v(13.1, 52.46) * mm, "end": v(12.92, 53.1) * mm});
            skLineSegment(sketch, "E1256", {"start": v(12.92, 53.1) * mm, "end": v(12.53, 53.84) * mm});
            skLineSegment(sketch, "E1257", {"start": v(12.53, 53.84) * mm, "end": v(11.98, 54.48) * mm});
            skLineSegment(sketch, "E1258", {"start": v(11.98, 54.48) * mm, "end": v(11.5, 54.88) * mm});
            skLineSegment(sketch, "E1259", {"start": v(11.5, 54.88) * mm, "end": v(11.32, 55) * mm});
            skLineSegment(sketch, "E1260", {"start": v(11.32, 55) * mm, "end": v(11.3, 55.15) * mm});
            skLineSegment(sketch, "E1261", {"start": v(11.3, 55.15) * mm, "end": v(11.03, 55.95) * mm});
            skLineSegment(sketch, "E1262", {"start": v(11.03, 55.95) * mm, "end": v(10.58, 56.74) * mm});
            skLineSegment(sketch, "E1263", {"start": v(10.58, 56.74) * mm, "end": v(10.46, 56.9) * mm});
            skLineSegment(sketch, "E1264", {"start": v(10.46, 56.9) * mm, "end": v(10.7, 57.08) * mm});
            skLineSegment(sketch, "E1265", {"start": v(10.7, 57.08) * mm, "end": v(11.36, 57.67) * mm});
            skLineSegment(sketch, "E1266", {"start": v(11.36, 57.67) * mm, "end": v(12.14, 58.5) * mm});
            skLineSegment(sketch, "E1267", {"start": v(12.14, 58.5) * mm, "end": v(12.82, 59.33) * mm});
            skLineSegment(sketch, "E1268", {"start": v(12.82, 59.33) * mm, "end": v(13.23, 59.88) * mm});
            skLineSegment(sketch, "E1269", {"start": v(13.23, 59.88) * mm, "end": v(13.37, 60.07) * mm});
            skLineSegment(sketch, "E1270", {"start": v(13.37, 60.07) * mm, "end": v(13.58, 60.35) * mm});
            skLineSegment(sketch, "E1271", {"start": v(13.58, 60.35) * mm, "end": v(14.22, 61.2) * mm});
            skLineSegment(sketch, "E1272", {"start": v(14.22, 61.2) * mm, "end": v(14.95, 62.12) * mm});
            skLineSegment(sketch, "E1273", {"start": v(14.95, 62.12) * mm, "end": v(15.58, 62.86) * mm});
            skLineSegment(sketch, "E1274", {"start": v(15.58, 62.86) * mm, "end": v(16.16, 63.44) * mm});
            skLineSegment(sketch, "E1275", {"start": v(16.16, 63.44) * mm, "end": v(16.7, 63.88) * mm});
            skLineSegment(sketch, "E1276", {"start": v(16.7, 63.88) * mm, "end": v(17.24, 64.2) * mm});
            skLineSegment(sketch, "E1277", {"start": v(17.24, 64.2) * mm, "end": v(17.8, 64.45) * mm});
            skLineSegment(sketch, "E1278", {"start": v(17.8, 64.45) * mm, "end": v(18.27, 64.6) * mm});
            skLineSegment(sketch, "E1279", {"start": v(18.27, 64.6) * mm, "end": v(18.43, 64.63) * mm});
            skLineSegment(sketch, "E1280", {"start": v(18.43, 64.63) * mm, "end": v(18.61, 64.67) * mm});
            skLineSegment(sketch, "E1281", {"start": v(18.61, 64.67) * mm, "end": v(19.1, 64.77) * mm});
            skLineSegment(sketch, "E1282", {"start": v(19.1, 64.77) * mm, "end": v(19.74, 64.87) * mm});
            skLineSegment(sketch, "E1283", {"start": v(19.74, 64.87) * mm, "end": v(20.26, 64.92) * mm});
            skLineSegment(sketch, "E1284", {"start": v(20.26, 64.92) * mm, "end": v(20.43, 64.92) * mm});
            skLineSegment(sketch, "E1285", {"start": v(20.43, 64.92) * mm, "end": v(20.75, 64.92) * mm});
            skLineSegment(sketch, "E1286", {"start": v(20.75, 64.92) * mm, "end": v(21.6, 65) * mm});
            skLineSegment(sketch, "E1287", {"start": v(21.6, 65) * mm, "end": v(21.7, 65.02) * mm});
            skLineSegment(sketch, "E1288", {"start": v(21.7, 65.02) * mm, "end": v(21.9, 65.05) * mm});
            skLineSegment(sketch, "E1289", {"start": v(21.9, 65.05) * mm, "end": v(22.44, 65.24) * mm});
            skLineSegment(sketch, "E1290", {"start": v(22.44, 65.24) * mm, "end": v(23.08, 65.6) * mm});
            skLineSegment(sketch, "E1291", {"start": v(23.08, 65.6) * mm, "end": v(23.63, 66.06) * mm});
            skLineSegment(sketch, "E1292", {"start": v(23.63, 66.06) * mm, "end": v(24.1, 66.58) * mm});
            skLineSegment(sketch, "E1293", {"start": v(24.1, 66.58) * mm, "end": v(24.47, 67.12) * mm});
            skLineSegment(sketch, "E1294", {"start": v(24.47, 67.12) * mm, "end": v(24.77, 67.64) * mm});
            skLineSegment(sketch, "E1295", {"start": v(24.77, 67.64) * mm, "end": v(25, 68.08) * mm});
            skLineSegment(sketch, "E1296", {"start": v(25, 68.08) * mm, "end": v(25.1, 68.33) * mm});
            skLineSegment(sketch, "E1297", {"start": v(25.1, 68.33) * mm, "end": v(25.14, 68.42) * mm});
            skLineSegment(sketch, "E1298", {"start": v(25.14, 68.42) * mm, "end": v(26.16, 70.96) * mm});
            skLineSegment(sketch, "E1299", {"start": v(26.16, 70.96) * mm, "end": v(26.32, 71.06) * mm});
            skLineSegment(sketch, "E1300", {"start": v(26.32, 71.06) * mm, "end": v(26.78, 71.43) * mm});
            skLineSegment(sketch, "E1301", {"start": v(26.78, 71.43) * mm, "end": v(27.3, 72.02) * mm});
            skLineSegment(sketch, "E1302", {"start": v(27.3, 72.02) * mm, "end": v(27.7, 72.68) * mm});
            skLineSegment(sketch, "E1303", {"start": v(27.7, 72.68) * mm, "end": v(28.03, 73.37) * mm});
            skLineSegment(sketch, "E1304", {"start": v(28.03, 73.37) * mm, "end": v(28.27, 74.04) * mm});
            skLineSegment(sketch, "E1305", {"start": v(28.27, 74.04) * mm, "end": v(28.43, 74.66) * mm});
            skLineSegment(sketch, "E1306", {"start": v(28.43, 74.66) * mm, "end": v(28.54, 75.2) * mm});
            skLineSegment(sketch, "E1307", {"start": v(28.54, 75.2) * mm, "end": v(28.6, 75.49) * mm});
            skLineSegment(sketch, "E1308", {"start": v(28.6, 75.49) * mm, "end": v(28.6, 75.59) * mm});
            skLineSegment(sketch, "E1309", {"start": v(28.6, 75.59) * mm, "end": v(29.16, 79.67) * mm});
            skLineSegment(sketch, "E1310", {"start": v(29.16, 79.67) * mm, "end": v(25.64, 77.54) * mm});
            skSolve(sketch);
        }
        {
            var Q0;
            Q0=makeQuery(id+"F21.imprint","IMPRINT",FACE,{"disambiguationData":[TD([[makeQuery(id+"F21.imprint","IMPRINT",EDGE,{"derivedFrom":sQuery(id+"F21.wireOp",EDGE,"E34")}),1.0]])]});
            extrude(context, id + "F22", {"entities" : qUnion([Q0]), "operationType" : NewBodyOperationType.ADD, "depth" : 2 * mm, "offsetDistance" : 25 * mm});
        }
    });
